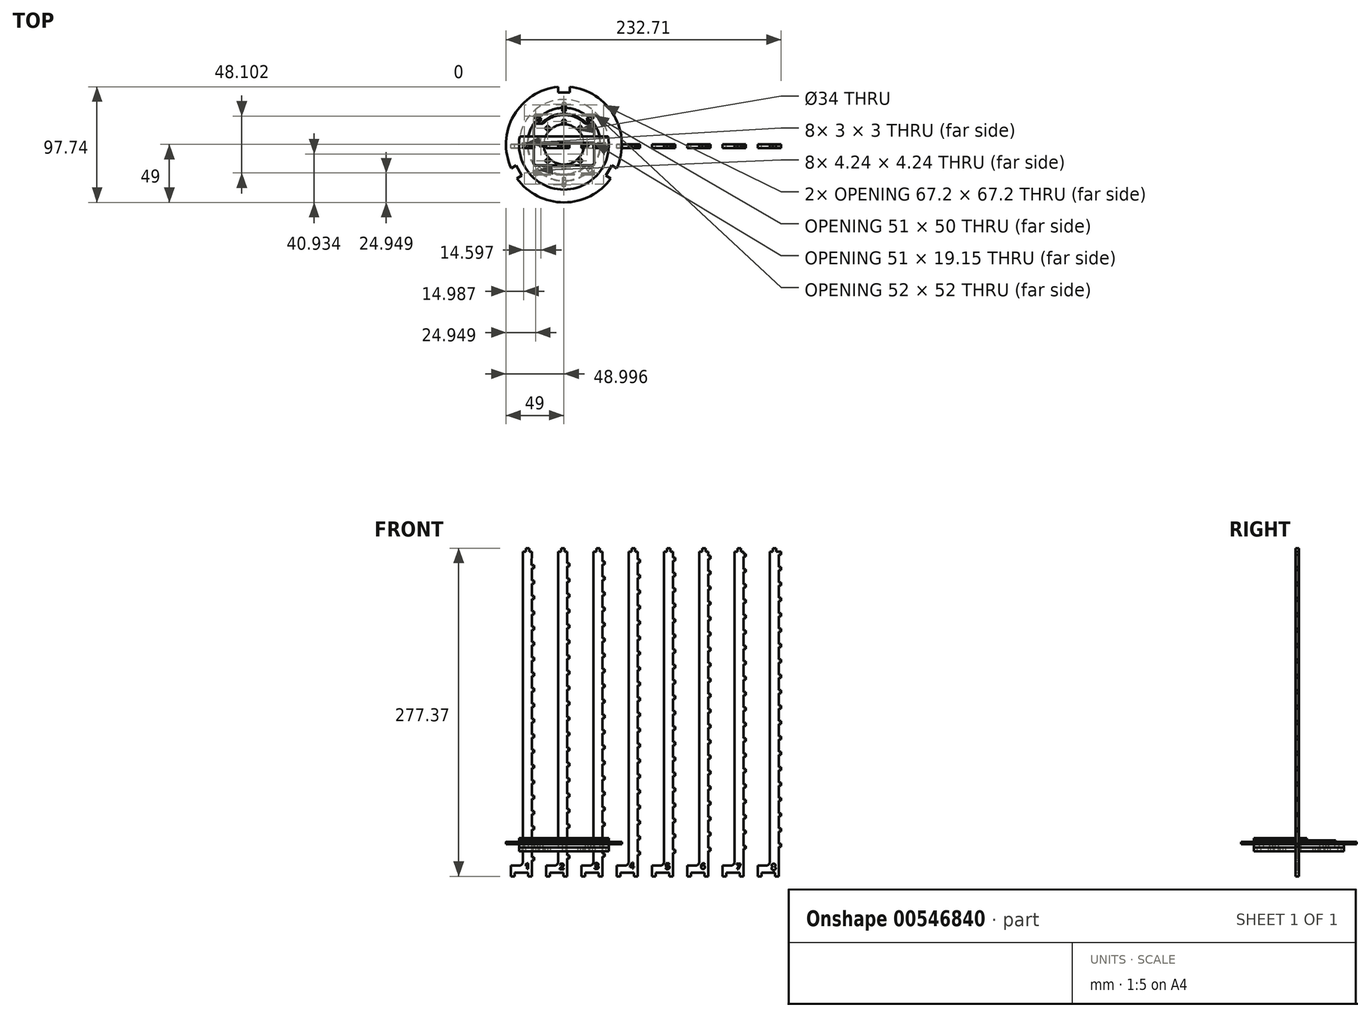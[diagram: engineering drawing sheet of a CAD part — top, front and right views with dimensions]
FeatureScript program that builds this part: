
annotation { "Feature Type Name" : "Feature", "Feature Type Description" : "" }
export const myFeature = defineFeature(function(context is Context, id is Id, definition is map)
    precondition{}
    {
        {
            assignVariable(context, id + "F0", {"name" : "thickness", "anyValue" : 3});
        }
        {
            var Q0;
            Q0=qCreatedBy(makeId("Front.planeOp"),FACE);
            var sketch = newSketch(context, id + "F1", { "sketchPlane" : qUnion([Q0])});
            skLineSegment(sketch, "E0", {"start": v(-27.17, -7.73) * mm, "end": v(-25.17, -7.73) * mm});
            skLineSegment(sketch, "E1", {"start": v(-25.17, -7.73) * mm, "end": v(-25.17, -5.23) * mm});
            skLineSegment(sketch, "E2", {"start": v(-25.17, -5.23) * mm, "end": v(-27.17, -5.23) * mm});
            skLineSegment(sketch, "E3.1.0.1", {"start": v(2.67, -6.1) * mm, "end": v(4.67, -6.1) * mm});
            skLineSegment(sketch, "E3.1.0.2", {"start": v(4.67, -6.1) * mm, "end": v(4.67, -3.6) * mm});
            skLineSegment(sketch, "E3.1.0.3", {"start": v(4.67, -3.6) * mm, "end": v(2.67, -3.6) * mm});
            skLineSegment(sketch, "E3.2.0.1", {"start": v(32.51, -4.48) * mm, "end": v(34.51, -4.48) * mm});
            skLineSegment(sketch, "E3.2.0.2", {"start": v(34.51, -4.48) * mm, "end": v(34.51, -1.98) * mm});
            skLineSegment(sketch, "E3.2.0.3", {"start": v(34.51, -1.98) * mm, "end": v(32.51, -1.98) * mm});
            skLineSegment(sketch, "E3.3.0.1", {"start": v(62.35, -2.86) * mm, "end": v(64.35, -2.86) * mm});
            skLineSegment(sketch, "E3.3.0.2", {"start": v(64.35, -2.86) * mm, "end": v(64.35, -0.36) * mm});
            skLineSegment(sketch, "E3.3.0.3", {"start": v(64.35, -0.36) * mm, "end": v(62.35, -0.36) * mm});
            skLineSegment(sketch, "E3.4.0.1", {"start": v(92.2, -1.23) * mm, "end": v(94.2, -1.23) * mm});
            skLineSegment(sketch, "E3.4.0.2", {"start": v(94.2, -1.23) * mm, "end": v(94.2, 1.27) * mm});
            skLineSegment(sketch, "E3.4.0.3", {"start": v(94.2, 1.27) * mm, "end": v(92.2, 1.27) * mm});
            skLineSegment(sketch, "E3.5.0.1", {"start": v(122.03, 0.4) * mm, "end": v(124.03, 0.4) * mm});
            skLineSegment(sketch, "E3.5.0.2", {"start": v(124.03, 0.4) * mm, "end": v(124.03, 2.9) * mm});
            skLineSegment(sketch, "E3.5.0.3", {"start": v(124.03, 2.9) * mm, "end": v(122.03, 2.9) * mm});
            skLineSegment(sketch, "E3.6.0.1", {"start": v(151.87, 2.02) * mm, "end": v(153.87, 2.02) * mm});
            skLineSegment(sketch, "E3.6.0.2", {"start": v(153.87, 2.02) * mm, "end": v(153.87, 4.52) * mm});
            skLineSegment(sketch, "E3.6.0.3", {"start": v(153.87, 4.52) * mm, "end": v(151.87, 4.52) * mm});
            skLineSegment(sketch, "E3.7.0.0", {"start": v(181.71, -18.23) * mm, "end": v(181.71, 3.64) * mm});
            skLineSegment(sketch, "E3.7.0.1", {"start": v(181.71, 3.64) * mm, "end": v(183.71, 3.64) * mm});
            skLineSegment(sketch, "E3.7.0.2", {"start": v(183.71, 3.64) * mm, "end": v(183.71, 6.14) * mm});
            skLineSegment(sketch, "E3.7.0.3", {"start": v(183.71, 6.14) * mm, "end": v(181.71, 6.14) * mm});
            skLineSegment(sketch, "E4.0.1.0", {"start": v(181.71, 6.14) * mm, "end": v(181.71, 16.64) * mm});
            skLineSegment(sketch, "E4.0.1.1", {"start": v(151.87, 4.52) * mm, "end": v(151.87, 15.02) * mm});
            skLineSegment(sketch, "E4.0.1.2", {"start": v(122.03, 2.9) * mm, "end": v(122.03, 13.4) * mm});
            skLineSegment(sketch, "E4.0.1.3", {"start": v(92.2, 1.27) * mm, "end": v(92.2, 11.77) * mm});
            skLineSegment(sketch, "E4.0.1.4", {"start": v(62.35, -0.36) * mm, "end": v(62.35, 10.14) * mm});
            skLineSegment(sketch, "E4.0.1.5", {"start": v(32.51, -1.98) * mm, "end": v(32.51, 8.52) * mm});
            skLineSegment(sketch, "E4.0.1.6", {"start": v(2.67, -3.6) * mm, "end": v(2.67, 6.9) * mm});
            skLineSegment(sketch, "E4.0.1.7", {"start": v(-27.17, -5.23) * mm, "end": v(-27.17, 5.27) * mm});
            skLineSegment(sketch, "E4.0.1.8", {"start": v(153.87, 17.52) * mm, "end": v(151.87, 17.52) * mm});
            skLineSegment(sketch, "E4.0.1.9", {"start": v(153.87, 15.02) * mm, "end": v(153.87, 17.52) * mm});
            skLineSegment(sketch, "E4.0.1.10", {"start": v(151.87, 15.02) * mm, "end": v(153.87, 15.02) * mm});
            skLineSegment(sketch, "E4.0.1.11", {"start": v(124.03, 15.9) * mm, "end": v(122.03, 15.9) * mm});
            skLineSegment(sketch, "E4.0.1.12", {"start": v(124.03, 13.4) * mm, "end": v(124.03, 15.9) * mm});
            skLineSegment(sketch, "E4.0.1.13", {"start": v(122.03, 13.4) * mm, "end": v(124.03, 13.4) * mm});
            skLineSegment(sketch, "E4.0.1.14", {"start": v(94.2, 14.27) * mm, "end": v(92.2, 14.27) * mm});
            skLineSegment(sketch, "E4.0.1.15", {"start": v(94.2, 11.77) * mm, "end": v(94.2, 14.27) * mm});
            skLineSegment(sketch, "E4.0.1.16", {"start": v(92.2, 11.77) * mm, "end": v(94.2, 11.77) * mm});
            skLineSegment(sketch, "E4.0.1.17", {"start": v(183.71, 19.14) * mm, "end": v(181.71, 19.14) * mm});
            skLineSegment(sketch, "E4.0.1.18", {"start": v(183.71, 16.64) * mm, "end": v(183.71, 19.14) * mm});
            skLineSegment(sketch, "E4.0.1.19", {"start": v(181.71, 16.64) * mm, "end": v(183.71, 16.64) * mm});
            skLineSegment(sketch, "E4.0.1.20", {"start": v(34.51, 11.02) * mm, "end": v(32.51, 11.02) * mm});
            skLineSegment(sketch, "E4.0.1.21", {"start": v(34.51, 8.52) * mm, "end": v(34.51, 11.02) * mm});
            skLineSegment(sketch, "E4.0.1.22", {"start": v(32.51, 8.52) * mm, "end": v(34.51, 8.52) * mm});
            skLineSegment(sketch, "E4.0.1.23", {"start": v(4.67, 9.4) * mm, "end": v(2.67, 9.4) * mm});
            skLineSegment(sketch, "E4.0.1.24", {"start": v(4.67, 6.9) * mm, "end": v(4.67, 9.4) * mm});
            skLineSegment(sketch, "E4.0.1.25", {"start": v(2.67, 6.9) * mm, "end": v(4.67, 6.9) * mm});
            skLineSegment(sketch, "E4.0.1.26", {"start": v(64.35, 12.64) * mm, "end": v(62.35, 12.64) * mm});
            skLineSegment(sketch, "E4.0.1.27", {"start": v(64.35, 10.14) * mm, "end": v(64.35, 12.64) * mm});
            skLineSegment(sketch, "E4.0.1.28", {"start": v(62.35, 10.14) * mm, "end": v(64.35, 10.14) * mm});
            skLineSegment(sketch, "E4.0.1.29", {"start": v(-25.17, 7.77) * mm, "end": v(-27.17, 7.77) * mm});
            skLineSegment(sketch, "E4.0.1.30", {"start": v(-25.17, 5.27) * mm, "end": v(-25.17, 7.77) * mm});
            skLineSegment(sketch, "E4.0.1.31", {"start": v(-27.17, 5.27) * mm, "end": v(-25.17, 5.27) * mm});
            skLineSegment(sketch, "E4.0.2.0", {"start": v(181.71, 19.14) * mm, "end": v(181.71, 29.64) * mm});
            skLineSegment(sketch, "E4.0.2.1", {"start": v(151.87, 17.52) * mm, "end": v(151.87, 28.02) * mm});
            skLineSegment(sketch, "E4.0.2.2", {"start": v(122.03, 15.9) * mm, "end": v(122.03, 26.4) * mm});
            skLineSegment(sketch, "E4.0.2.3", {"start": v(92.2, 14.27) * mm, "end": v(92.2, 24.77) * mm});
            skLineSegment(sketch, "E4.0.2.4", {"start": v(62.35, 12.64) * mm, "end": v(62.35, 23.14) * mm});
            skLineSegment(sketch, "E4.0.2.5", {"start": v(32.51, 11.02) * mm, "end": v(32.51, 21.52) * mm});
            skLineSegment(sketch, "E4.0.2.6", {"start": v(2.67, 9.4) * mm, "end": v(2.67, 19.9) * mm});
            skLineSegment(sketch, "E4.0.2.7", {"start": v(-27.17, 7.77) * mm, "end": v(-27.17, 18.27) * mm});
            skLineSegment(sketch, "E4.0.2.8", {"start": v(153.87, 30.52) * mm, "end": v(151.87, 30.52) * mm});
            skLineSegment(sketch, "E4.0.2.9", {"start": v(153.87, 28.02) * mm, "end": v(153.87, 30.52) * mm});
            skLineSegment(sketch, "E4.0.2.10", {"start": v(151.87, 28.02) * mm, "end": v(153.87, 28.02) * mm});
            skLineSegment(sketch, "E4.0.2.11", {"start": v(124.03, 28.9) * mm, "end": v(122.03, 28.9) * mm});
            skLineSegment(sketch, "E4.0.2.12", {"start": v(124.03, 26.4) * mm, "end": v(124.03, 28.9) * mm});
            skLineSegment(sketch, "E4.0.2.13", {"start": v(122.03, 26.4) * mm, "end": v(124.03, 26.4) * mm});
            skLineSegment(sketch, "E4.0.2.14", {"start": v(94.2, 27.27) * mm, "end": v(92.2, 27.27) * mm});
            skLineSegment(sketch, "E4.0.2.15", {"start": v(94.2, 24.77) * mm, "end": v(94.2, 27.27) * mm});
            skLineSegment(sketch, "E4.0.2.16", {"start": v(92.2, 24.77) * mm, "end": v(94.2, 24.77) * mm});
            skLineSegment(sketch, "E4.0.2.17", {"start": v(183.71, 32.14) * mm, "end": v(181.71, 32.14) * mm});
            skLineSegment(sketch, "E4.0.2.18", {"start": v(183.71, 29.64) * mm, "end": v(183.71, 32.14) * mm});
            skLineSegment(sketch, "E4.0.2.19", {"start": v(181.71, 29.64) * mm, "end": v(183.71, 29.64) * mm});
            skLineSegment(sketch, "E4.0.2.20", {"start": v(34.51, 24.02) * mm, "end": v(32.51, 24.02) * mm});
            skLineSegment(sketch, "E4.0.2.21", {"start": v(34.51, 21.52) * mm, "end": v(34.51, 24.02) * mm});
            skLineSegment(sketch, "E4.0.2.22", {"start": v(32.51, 21.52) * mm, "end": v(34.51, 21.52) * mm});
            skLineSegment(sketch, "E4.0.2.23", {"start": v(4.67, 22.4) * mm, "end": v(2.67, 22.4) * mm});
            skLineSegment(sketch, "E4.0.2.24", {"start": v(4.67, 19.9) * mm, "end": v(4.67, 22.4) * mm});
            skLineSegment(sketch, "E4.0.2.25", {"start": v(2.67, 19.9) * mm, "end": v(4.67, 19.9) * mm});
            skLineSegment(sketch, "E4.0.2.26", {"start": v(64.35, 25.64) * mm, "end": v(62.35, 25.64) * mm});
            skLineSegment(sketch, "E4.0.2.27", {"start": v(64.35, 23.14) * mm, "end": v(64.35, 25.64) * mm});
            skLineSegment(sketch, "E4.0.2.28", {"start": v(62.35, 23.14) * mm, "end": v(64.35, 23.14) * mm});
            skLineSegment(sketch, "E4.0.2.29", {"start": v(-25.17, 20.77) * mm, "end": v(-27.17, 20.77) * mm});
            skLineSegment(sketch, "E4.0.2.30", {"start": v(-25.17, 18.27) * mm, "end": v(-25.17, 20.77) * mm});
            skLineSegment(sketch, "E4.0.2.31", {"start": v(-27.17, 18.27) * mm, "end": v(-25.17, 18.27) * mm});
            skLineSegment(sketch, "E4.0.3.0", {"start": v(181.71, 32.14) * mm, "end": v(181.71, 42.64) * mm});
            skLineSegment(sketch, "E4.0.3.1", {"start": v(151.87, 30.52) * mm, "end": v(151.87, 41.02) * mm});
            skLineSegment(sketch, "E4.0.3.2", {"start": v(122.03, 28.9) * mm, "end": v(122.03, 39.4) * mm});
            skLineSegment(sketch, "E4.0.3.3", {"start": v(92.2, 27.27) * mm, "end": v(92.2, 37.77) * mm});
            skLineSegment(sketch, "E4.0.3.4", {"start": v(62.35, 25.64) * mm, "end": v(62.35, 36.14) * mm});
            skLineSegment(sketch, "E4.0.3.5", {"start": v(32.51, 24.02) * mm, "end": v(32.51, 34.52) * mm});
            skLineSegment(sketch, "E4.0.3.6", {"start": v(2.67, 22.4) * mm, "end": v(2.67, 32.9) * mm});
            skLineSegment(sketch, "E4.0.3.7", {"start": v(-27.17, 20.77) * mm, "end": v(-27.17, 31.27) * mm});
            skLineSegment(sketch, "E4.0.3.8", {"start": v(153.87, 43.52) * mm, "end": v(151.87, 43.52) * mm});
            skLineSegment(sketch, "E4.0.3.9", {"start": v(153.87, 41.02) * mm, "end": v(153.87, 43.52) * mm});
            skLineSegment(sketch, "E4.0.3.10", {"start": v(151.87, 41.02) * mm, "end": v(153.87, 41.02) * mm});
            skLineSegment(sketch, "E4.0.3.11", {"start": v(124.03, 41.9) * mm, "end": v(122.03, 41.9) * mm});
            skLineSegment(sketch, "E4.0.3.12", {"start": v(124.03, 39.4) * mm, "end": v(124.03, 41.9) * mm});
            skLineSegment(sketch, "E4.0.3.13", {"start": v(122.03, 39.4) * mm, "end": v(124.03, 39.4) * mm});
            skLineSegment(sketch, "E4.0.3.14", {"start": v(94.2, 40.27) * mm, "end": v(92.2, 40.27) * mm});
            skLineSegment(sketch, "E4.0.3.15", {"start": v(94.2, 37.77) * mm, "end": v(94.2, 40.27) * mm});
            skLineSegment(sketch, "E4.0.3.16", {"start": v(92.2, 37.77) * mm, "end": v(94.2, 37.77) * mm});
            skLineSegment(sketch, "E4.0.3.17", {"start": v(183.71, 45.14) * mm, "end": v(181.71, 45.14) * mm});
            skLineSegment(sketch, "E4.0.3.18", {"start": v(183.71, 42.64) * mm, "end": v(183.71, 45.14) * mm});
            skLineSegment(sketch, "E4.0.3.19", {"start": v(181.71, 42.64) * mm, "end": v(183.71, 42.64) * mm});
            skLineSegment(sketch, "E4.0.3.20", {"start": v(34.51, 37.02) * mm, "end": v(32.51, 37.02) * mm});
            skLineSegment(sketch, "E4.0.3.21", {"start": v(34.51, 34.52) * mm, "end": v(34.51, 37.02) * mm});
            skLineSegment(sketch, "E4.0.3.22", {"start": v(32.51, 34.52) * mm, "end": v(34.51, 34.52) * mm});
            skLineSegment(sketch, "E4.0.3.23", {"start": v(4.67, 35.4) * mm, "end": v(2.67, 35.4) * mm});
            skLineSegment(sketch, "E4.0.3.24", {"start": v(4.67, 32.9) * mm, "end": v(4.67, 35.4) * mm});
            skLineSegment(sketch, "E4.0.3.25", {"start": v(2.67, 32.9) * mm, "end": v(4.67, 32.9) * mm});
            skLineSegment(sketch, "E4.0.3.26", {"start": v(64.35, 38.64) * mm, "end": v(62.35, 38.64) * mm});
            skLineSegment(sketch, "E4.0.3.27", {"start": v(64.35, 36.14) * mm, "end": v(64.35, 38.64) * mm});
            skLineSegment(sketch, "E4.0.3.28", {"start": v(62.35, 36.14) * mm, "end": v(64.35, 36.14) * mm});
            skLineSegment(sketch, "E4.0.3.29", {"start": v(-25.17, 33.77) * mm, "end": v(-27.17, 33.77) * mm});
            skLineSegment(sketch, "E4.0.3.30", {"start": v(-25.17, 31.27) * mm, "end": v(-25.17, 33.77) * mm});
            skLineSegment(sketch, "E4.0.3.31", {"start": v(-27.17, 31.27) * mm, "end": v(-25.17, 31.27) * mm});
            skLineSegment(sketch, "E4.0.4.0", {"start": v(181.71, 45.14) * mm, "end": v(181.71, 55.64) * mm});
            skLineSegment(sketch, "E4.0.4.1", {"start": v(151.87, 43.52) * mm, "end": v(151.87, 54.02) * mm});
            skLineSegment(sketch, "E4.0.4.2", {"start": v(122.03, 41.9) * mm, "end": v(122.03, 52.4) * mm});
            skLineSegment(sketch, "E4.0.4.3", {"start": v(92.2, 40.27) * mm, "end": v(92.2, 50.77) * mm});
            skLineSegment(sketch, "E4.0.4.4", {"start": v(62.35, 38.64) * mm, "end": v(62.35, 49.14) * mm});
            skLineSegment(sketch, "E4.0.4.5", {"start": v(32.51, 37.02) * mm, "end": v(32.51, 47.52) * mm});
            skLineSegment(sketch, "E4.0.4.6", {"start": v(2.67, 35.4) * mm, "end": v(2.67, 45.9) * mm});
            skLineSegment(sketch, "E4.0.4.7", {"start": v(-27.17, 33.77) * mm, "end": v(-27.17, 44.27) * mm});
            skLineSegment(sketch, "E4.0.4.8", {"start": v(153.87, 56.52) * mm, "end": v(151.87, 56.52) * mm});
            skLineSegment(sketch, "E4.0.4.9", {"start": v(153.87, 54.02) * mm, "end": v(153.87, 56.52) * mm});
            skLineSegment(sketch, "E4.0.4.10", {"start": v(151.87, 54.02) * mm, "end": v(153.87, 54.02) * mm});
            skLineSegment(sketch, "E4.0.4.11", {"start": v(124.03, 54.9) * mm, "end": v(122.03, 54.9) * mm});
            skLineSegment(sketch, "E4.0.4.12", {"start": v(124.03, 52.4) * mm, "end": v(124.03, 54.9) * mm});
            skLineSegment(sketch, "E4.0.4.13", {"start": v(122.03, 52.4) * mm, "end": v(124.03, 52.4) * mm});
            skLineSegment(sketch, "E4.0.4.14", {"start": v(94.2, 53.27) * mm, "end": v(92.2, 53.27) * mm});
            skLineSegment(sketch, "E4.0.4.15", {"start": v(94.2, 50.77) * mm, "end": v(94.2, 53.27) * mm});
            skLineSegment(sketch, "E4.0.4.16", {"start": v(92.2, 50.77) * mm, "end": v(94.2, 50.77) * mm});
            skLineSegment(sketch, "E4.0.4.17", {"start": v(183.71, 58.14) * mm, "end": v(181.71, 58.14) * mm});
            skLineSegment(sketch, "E4.0.4.18", {"start": v(183.71, 55.64) * mm, "end": v(183.71, 58.14) * mm});
            skLineSegment(sketch, "E4.0.4.19", {"start": v(181.71, 55.64) * mm, "end": v(183.71, 55.64) * mm});
            skLineSegment(sketch, "E4.0.4.20", {"start": v(34.51, 50.02) * mm, "end": v(32.51, 50.02) * mm});
            skLineSegment(sketch, "E4.0.4.21", {"start": v(34.51, 47.52) * mm, "end": v(34.51, 50.02) * mm});
            skLineSegment(sketch, "E4.0.4.22", {"start": v(32.51, 47.52) * mm, "end": v(34.51, 47.52) * mm});
            skLineSegment(sketch, "E4.0.4.23", {"start": v(4.67, 48.4) * mm, "end": v(2.67, 48.4) * mm});
            skLineSegment(sketch, "E4.0.4.24", {"start": v(4.67, 45.9) * mm, "end": v(4.67, 48.4) * mm});
            skLineSegment(sketch, "E4.0.4.25", {"start": v(2.67, 45.9) * mm, "end": v(4.67, 45.9) * mm});
            skLineSegment(sketch, "E4.0.4.26", {"start": v(64.35, 51.64) * mm, "end": v(62.35, 51.64) * mm});
            skLineSegment(sketch, "E4.0.4.27", {"start": v(64.35, 49.14) * mm, "end": v(64.35, 51.64) * mm});
            skLineSegment(sketch, "E4.0.4.28", {"start": v(62.35, 49.14) * mm, "end": v(64.35, 49.14) * mm});
            skLineSegment(sketch, "E4.0.4.29", {"start": v(-25.17, 46.77) * mm, "end": v(-27.17, 46.77) * mm});
            skLineSegment(sketch, "E4.0.4.30", {"start": v(-25.17, 44.27) * mm, "end": v(-25.17, 46.77) * mm});
            skLineSegment(sketch, "E4.0.4.31", {"start": v(-27.17, 44.27) * mm, "end": v(-25.17, 44.27) * mm});
            skLineSegment(sketch, "E4.0.5.0", {"start": v(181.71, 58.14) * mm, "end": v(181.71, 68.64) * mm});
            skLineSegment(sketch, "E4.0.5.1", {"start": v(151.87, 56.52) * mm, "end": v(151.87, 67.02) * mm});
            skLineSegment(sketch, "E4.0.5.2", {"start": v(122.03, 54.9) * mm, "end": v(122.03, 65.4) * mm});
            skLineSegment(sketch, "E4.0.5.3", {"start": v(92.2, 53.27) * mm, "end": v(92.2, 63.77) * mm});
            skLineSegment(sketch, "E4.0.5.4", {"start": v(62.35, 51.64) * mm, "end": v(62.35, 62.14) * mm});
            skLineSegment(sketch, "E4.0.5.5", {"start": v(32.51, 50.02) * mm, "end": v(32.51, 60.52) * mm});
            skLineSegment(sketch, "E4.0.5.6", {"start": v(2.67, 48.4) * mm, "end": v(2.67, 58.9) * mm});
            skLineSegment(sketch, "E4.0.5.7", {"start": v(-27.17, 46.77) * mm, "end": v(-27.17, 57.27) * mm});
            skLineSegment(sketch, "E4.0.5.8", {"start": v(153.87, 69.52) * mm, "end": v(151.87, 69.52) * mm});
            skLineSegment(sketch, "E4.0.5.9", {"start": v(153.87, 67.02) * mm, "end": v(153.87, 69.52) * mm});
            skLineSegment(sketch, "E4.0.5.10", {"start": v(151.87, 67.02) * mm, "end": v(153.87, 67.02) * mm});
            skLineSegment(sketch, "E4.0.5.11", {"start": v(124.03, 67.9) * mm, "end": v(122.03, 67.9) * mm});
            skLineSegment(sketch, "E4.0.5.12", {"start": v(124.03, 65.4) * mm, "end": v(124.03, 67.9) * mm});
            skLineSegment(sketch, "E4.0.5.13", {"start": v(122.03, 65.4) * mm, "end": v(124.03, 65.4) * mm});
            skLineSegment(sketch, "E4.0.5.14", {"start": v(94.2, 66.27) * mm, "end": v(92.2, 66.27) * mm});
            skLineSegment(sketch, "E4.0.5.15", {"start": v(94.2, 63.77) * mm, "end": v(94.2, 66.27) * mm});
            skLineSegment(sketch, "E4.0.5.16", {"start": v(92.2, 63.77) * mm, "end": v(94.2, 63.77) * mm});
            skLineSegment(sketch, "E4.0.5.17", {"start": v(183.71, 71.14) * mm, "end": v(181.71, 71.14) * mm});
            skLineSegment(sketch, "E4.0.5.18", {"start": v(183.71, 68.64) * mm, "end": v(183.71, 71.14) * mm});
            skLineSegment(sketch, "E4.0.5.19", {"start": v(181.71, 68.64) * mm, "end": v(183.71, 68.64) * mm});
            skLineSegment(sketch, "E4.0.5.20", {"start": v(34.51, 63.02) * mm, "end": v(32.51, 63.02) * mm});
            skLineSegment(sketch, "E4.0.5.21", {"start": v(34.51, 60.52) * mm, "end": v(34.51, 63.02) * mm});
            skLineSegment(sketch, "E4.0.5.22", {"start": v(32.51, 60.52) * mm, "end": v(34.51, 60.52) * mm});
            skLineSegment(sketch, "E4.0.5.23", {"start": v(4.67, 61.4) * mm, "end": v(2.67, 61.4) * mm});
            skLineSegment(sketch, "E4.0.5.24", {"start": v(4.67, 58.9) * mm, "end": v(4.67, 61.4) * mm});
            skLineSegment(sketch, "E4.0.5.25", {"start": v(2.67, 58.9) * mm, "end": v(4.67, 58.9) * mm});
            skLineSegment(sketch, "E4.0.5.26", {"start": v(64.35, 64.64) * mm, "end": v(62.35, 64.64) * mm});
            skLineSegment(sketch, "E4.0.5.27", {"start": v(64.35, 62.14) * mm, "end": v(64.35, 64.64) * mm});
            skLineSegment(sketch, "E4.0.5.28", {"start": v(62.35, 62.14) * mm, "end": v(64.35, 62.14) * mm});
            skLineSegment(sketch, "E4.0.5.29", {"start": v(-25.17, 59.77) * mm, "end": v(-27.17, 59.77) * mm});
            skLineSegment(sketch, "E4.0.5.30", {"start": v(-25.17, 57.27) * mm, "end": v(-25.17, 59.77) * mm});
            skLineSegment(sketch, "E4.0.5.31", {"start": v(-27.17, 57.27) * mm, "end": v(-25.17, 57.27) * mm});
            skLineSegment(sketch, "E4.0.6.0", {"start": v(181.71, 71.14) * mm, "end": v(181.71, 81.64) * mm});
            skLineSegment(sketch, "E4.0.6.1", {"start": v(151.87, 69.52) * mm, "end": v(151.87, 80.02) * mm});
            skLineSegment(sketch, "E4.0.6.2", {"start": v(122.03, 67.9) * mm, "end": v(122.03, 78.4) * mm});
            skLineSegment(sketch, "E4.0.6.3", {"start": v(92.2, 66.27) * mm, "end": v(92.2, 76.77) * mm});
            skLineSegment(sketch, "E4.0.6.4", {"start": v(62.35, 64.64) * mm, "end": v(62.35, 75.14) * mm});
            skLineSegment(sketch, "E4.0.6.5", {"start": v(32.51, 63.02) * mm, "end": v(32.51, 73.52) * mm});
            skLineSegment(sketch, "E4.0.6.6", {"start": v(2.67, 61.4) * mm, "end": v(2.67, 71.9) * mm});
            skLineSegment(sketch, "E4.0.6.7", {"start": v(-27.17, 59.77) * mm, "end": v(-27.17, 70.27) * mm});
            skLineSegment(sketch, "E4.0.6.8", {"start": v(153.87, 82.52) * mm, "end": v(151.87, 82.52) * mm});
            skLineSegment(sketch, "E4.0.6.9", {"start": v(153.87, 80.02) * mm, "end": v(153.87, 82.52) * mm});
            skLineSegment(sketch, "E4.0.6.10", {"start": v(151.87, 80.02) * mm, "end": v(153.87, 80.02) * mm});
            skLineSegment(sketch, "E4.0.6.11", {"start": v(124.03, 80.9) * mm, "end": v(122.03, 80.9) * mm});
            skLineSegment(sketch, "E4.0.6.12", {"start": v(124.03, 78.4) * mm, "end": v(124.03, 80.9) * mm});
            skLineSegment(sketch, "E4.0.6.13", {"start": v(122.03, 78.4) * mm, "end": v(124.03, 78.4) * mm});
            skLineSegment(sketch, "E4.0.6.14", {"start": v(94.2, 79.27) * mm, "end": v(92.2, 79.27) * mm});
            skLineSegment(sketch, "E4.0.6.15", {"start": v(94.2, 76.77) * mm, "end": v(94.2, 79.27) * mm});
            skLineSegment(sketch, "E4.0.6.16", {"start": v(92.2, 76.77) * mm, "end": v(94.2, 76.77) * mm});
            skLineSegment(sketch, "E4.0.6.17", {"start": v(183.71, 84.14) * mm, "end": v(181.71, 84.14) * mm});
            skLineSegment(sketch, "E4.0.6.18", {"start": v(183.71, 81.64) * mm, "end": v(183.71, 84.14) * mm});
            skLineSegment(sketch, "E4.0.6.19", {"start": v(181.71, 81.64) * mm, "end": v(183.71, 81.64) * mm});
            skLineSegment(sketch, "E4.0.6.20", {"start": v(34.51, 76.02) * mm, "end": v(32.51, 76.02) * mm});
            skLineSegment(sketch, "E4.0.6.21", {"start": v(34.51, 73.52) * mm, "end": v(34.51, 76.02) * mm});
            skLineSegment(sketch, "E4.0.6.22", {"start": v(32.51, 73.52) * mm, "end": v(34.51, 73.52) * mm});
            skLineSegment(sketch, "E4.0.6.23", {"start": v(4.67, 74.4) * mm, "end": v(2.67, 74.4) * mm});
            skLineSegment(sketch, "E4.0.6.24", {"start": v(4.67, 71.9) * mm, "end": v(4.67, 74.4) * mm});
            skLineSegment(sketch, "E4.0.6.25", {"start": v(2.67, 71.9) * mm, "end": v(4.67, 71.9) * mm});
            skLineSegment(sketch, "E4.0.6.26", {"start": v(64.35, 77.64) * mm, "end": v(62.35, 77.64) * mm});
            skLineSegment(sketch, "E4.0.6.27", {"start": v(64.35, 75.14) * mm, "end": v(64.35, 77.64) * mm});
            skLineSegment(sketch, "E4.0.6.28", {"start": v(62.35, 75.14) * mm, "end": v(64.35, 75.14) * mm});
            skLineSegment(sketch, "E4.0.6.29", {"start": v(-25.17, 72.77) * mm, "end": v(-27.17, 72.77) * mm});
            skLineSegment(sketch, "E4.0.6.30", {"start": v(-25.17, 70.27) * mm, "end": v(-25.17, 72.77) * mm});
            skLineSegment(sketch, "E4.0.6.31", {"start": v(-27.17, 70.27) * mm, "end": v(-25.17, 70.27) * mm});
            skLineSegment(sketch, "E4.0.7.0", {"start": v(181.71, 84.14) * mm, "end": v(181.71, 94.64) * mm});
            skLineSegment(sketch, "E4.0.7.1", {"start": v(151.87, 82.52) * mm, "end": v(151.87, 93.02) * mm});
            skLineSegment(sketch, "E4.0.7.2", {"start": v(122.03, 80.9) * mm, "end": v(122.03, 91.4) * mm});
            skLineSegment(sketch, "E4.0.7.3", {"start": v(92.2, 79.27) * mm, "end": v(92.2, 89.77) * mm});
            skLineSegment(sketch, "E4.0.7.4", {"start": v(62.35, 77.64) * mm, "end": v(62.35, 88.14) * mm});
            skLineSegment(sketch, "E4.0.7.5", {"start": v(32.51, 76.02) * mm, "end": v(32.51, 86.52) * mm});
            skLineSegment(sketch, "E4.0.7.6", {"start": v(2.67, 74.4) * mm, "end": v(2.67, 84.9) * mm});
            skLineSegment(sketch, "E4.0.7.7", {"start": v(-27.17, 72.77) * mm, "end": v(-27.17, 83.27) * mm});
            skLineSegment(sketch, "E4.0.7.8", {"start": v(153.87, 95.52) * mm, "end": v(151.87, 95.52) * mm});
            skLineSegment(sketch, "E4.0.7.9", {"start": v(153.87, 93.02) * mm, "end": v(153.87, 95.52) * mm});
            skLineSegment(sketch, "E4.0.7.10", {"start": v(151.87, 93.02) * mm, "end": v(153.87, 93.02) * mm});
            skLineSegment(sketch, "E4.0.7.11", {"start": v(124.03, 93.9) * mm, "end": v(122.03, 93.9) * mm});
            skLineSegment(sketch, "E4.0.7.12", {"start": v(124.03, 91.4) * mm, "end": v(124.03, 93.9) * mm});
            skLineSegment(sketch, "E4.0.7.13", {"start": v(122.03, 91.4) * mm, "end": v(124.03, 91.4) * mm});
            skLineSegment(sketch, "E4.0.7.14", {"start": v(94.2, 92.27) * mm, "end": v(92.2, 92.27) * mm});
            skLineSegment(sketch, "E4.0.7.15", {"start": v(94.2, 89.77) * mm, "end": v(94.2, 92.27) * mm});
            skLineSegment(sketch, "E4.0.7.16", {"start": v(92.2, 89.77) * mm, "end": v(94.2, 89.77) * mm});
            skLineSegment(sketch, "E4.0.7.17", {"start": v(183.71, 97.14) * mm, "end": v(181.71, 97.14) * mm});
            skLineSegment(sketch, "E4.0.7.18", {"start": v(183.71, 94.64) * mm, "end": v(183.71, 97.14) * mm});
            skLineSegment(sketch, "E4.0.7.19", {"start": v(181.71, 94.64) * mm, "end": v(183.71, 94.64) * mm});
            skLineSegment(sketch, "E4.0.7.20", {"start": v(34.51, 89.02) * mm, "end": v(32.51, 89.02) * mm});
            skLineSegment(sketch, "E4.0.7.21", {"start": v(34.51, 86.52) * mm, "end": v(34.51, 89.02) * mm});
            skLineSegment(sketch, "E4.0.7.22", {"start": v(32.51, 86.52) * mm, "end": v(34.51, 86.52) * mm});
            skLineSegment(sketch, "E4.0.7.23", {"start": v(4.67, 87.4) * mm, "end": v(2.67, 87.4) * mm});
            skLineSegment(sketch, "E4.0.7.24", {"start": v(4.67, 84.9) * mm, "end": v(4.67, 87.4) * mm});
            skLineSegment(sketch, "E4.0.7.25", {"start": v(2.67, 84.9) * mm, "end": v(4.67, 84.9) * mm});
            skLineSegment(sketch, "E4.0.7.26", {"start": v(64.35, 90.64) * mm, "end": v(62.35, 90.64) * mm});
            skLineSegment(sketch, "E4.0.7.27", {"start": v(64.35, 88.14) * mm, "end": v(64.35, 90.64) * mm});
            skLineSegment(sketch, "E4.0.7.28", {"start": v(62.35, 88.14) * mm, "end": v(64.35, 88.14) * mm});
            skLineSegment(sketch, "E4.0.7.29", {"start": v(-25.17, 85.77) * mm, "end": v(-27.17, 85.77) * mm});
            skLineSegment(sketch, "E4.0.7.30", {"start": v(-25.17, 83.27) * mm, "end": v(-25.17, 85.77) * mm});
            skLineSegment(sketch, "E4.0.7.31", {"start": v(-27.17, 83.27) * mm, "end": v(-25.17, 83.27) * mm});
            skLineSegment(sketch, "E4.0.8.0", {"start": v(181.71, 97.14) * mm, "end": v(181.71, 107.64) * mm});
            skLineSegment(sketch, "E4.0.8.1", {"start": v(151.87, 95.52) * mm, "end": v(151.87, 106.02) * mm});
            skLineSegment(sketch, "E4.0.8.2", {"start": v(122.03, 93.9) * mm, "end": v(122.03, 104.4) * mm});
            skLineSegment(sketch, "E4.0.8.3", {"start": v(92.2, 92.27) * mm, "end": v(92.2, 102.77) * mm});
            skLineSegment(sketch, "E4.0.8.4", {"start": v(62.35, 90.64) * mm, "end": v(62.35, 101.14) * mm});
            skLineSegment(sketch, "E4.0.8.5", {"start": v(32.51, 89.02) * mm, "end": v(32.51, 99.52) * mm});
            skLineSegment(sketch, "E4.0.8.6", {"start": v(2.67, 87.4) * mm, "end": v(2.67, 97.9) * mm});
            skLineSegment(sketch, "E4.0.8.7", {"start": v(-27.17, 85.77) * mm, "end": v(-27.17, 96.27) * mm});
            skLineSegment(sketch, "E4.0.8.8", {"start": v(153.87, 108.52) * mm, "end": v(151.87, 108.52) * mm});
            skLineSegment(sketch, "E4.0.8.9", {"start": v(153.87, 106.02) * mm, "end": v(153.87, 108.52) * mm});
            skLineSegment(sketch, "E4.0.8.10", {"start": v(151.87, 106.02) * mm, "end": v(153.87, 106.02) * mm});
            skLineSegment(sketch, "E4.0.8.11", {"start": v(124.03, 106.9) * mm, "end": v(122.03, 106.9) * mm});
            skLineSegment(sketch, "E4.0.8.12", {"start": v(124.03, 104.4) * mm, "end": v(124.03, 106.9) * mm});
            skLineSegment(sketch, "E4.0.8.13", {"start": v(122.03, 104.4) * mm, "end": v(124.03, 104.4) * mm});
            skLineSegment(sketch, "E4.0.8.14", {"start": v(94.2, 105.27) * mm, "end": v(92.2, 105.27) * mm});
            skLineSegment(sketch, "E4.0.8.15", {"start": v(94.2, 102.77) * mm, "end": v(94.2, 105.27) * mm});
            skLineSegment(sketch, "E4.0.8.16", {"start": v(92.2, 102.77) * mm, "end": v(94.2, 102.77) * mm});
            skLineSegment(sketch, "E4.0.8.17", {"start": v(183.71, 110.14) * mm, "end": v(181.71, 110.14) * mm});
            skLineSegment(sketch, "E4.0.8.18", {"start": v(183.71, 107.64) * mm, "end": v(183.71, 110.14) * mm});
            skLineSegment(sketch, "E4.0.8.19", {"start": v(181.71, 107.64) * mm, "end": v(183.71, 107.64) * mm});
            skLineSegment(sketch, "E4.0.8.20", {"start": v(34.51, 102.02) * mm, "end": v(32.51, 102.02) * mm});
            skLineSegment(sketch, "E4.0.8.21", {"start": v(34.51, 99.52) * mm, "end": v(34.51, 102.02) * mm});
            skLineSegment(sketch, "E4.0.8.22", {"start": v(32.51, 99.52) * mm, "end": v(34.51, 99.52) * mm});
            skLineSegment(sketch, "E4.0.8.23", {"start": v(4.67, 100.4) * mm, "end": v(2.67, 100.4) * mm});
            skLineSegment(sketch, "E4.0.8.24", {"start": v(4.67, 97.9) * mm, "end": v(4.67, 100.4) * mm});
            skLineSegment(sketch, "E4.0.8.25", {"start": v(2.67, 97.9) * mm, "end": v(4.67, 97.9) * mm});
            skLineSegment(sketch, "E4.0.8.26", {"start": v(64.35, 103.64) * mm, "end": v(62.35, 103.64) * mm});
            skLineSegment(sketch, "E4.0.8.27", {"start": v(64.35, 101.14) * mm, "end": v(64.35, 103.64) * mm});
            skLineSegment(sketch, "E4.0.8.28", {"start": v(62.35, 101.14) * mm, "end": v(64.35, 101.14) * mm});
            skLineSegment(sketch, "E4.0.8.29", {"start": v(-25.17, 98.77) * mm, "end": v(-27.17, 98.77) * mm});
            skLineSegment(sketch, "E4.0.8.30", {"start": v(-25.17, 96.27) * mm, "end": v(-25.17, 98.77) * mm});
            skLineSegment(sketch, "E4.0.8.31", {"start": v(-27.17, 96.27) * mm, "end": v(-25.17, 96.27) * mm});
            skLineSegment(sketch, "E4.0.9.0", {"start": v(181.71, 110.14) * mm, "end": v(181.71, 120.64) * mm});
            skLineSegment(sketch, "E4.0.9.1", {"start": v(151.87, 108.52) * mm, "end": v(151.87, 119.02) * mm});
            skLineSegment(sketch, "E4.0.9.2", {"start": v(122.03, 106.9) * mm, "end": v(122.03, 117.4) * mm});
            skLineSegment(sketch, "E4.0.9.3", {"start": v(92.2, 105.27) * mm, "end": v(92.2, 115.77) * mm});
            skLineSegment(sketch, "E4.0.9.4", {"start": v(62.35, 103.64) * mm, "end": v(62.35, 114.14) * mm});
            skLineSegment(sketch, "E4.0.9.5", {"start": v(32.51, 102.02) * mm, "end": v(32.51, 112.52) * mm});
            skLineSegment(sketch, "E4.0.9.6", {"start": v(2.67, 100.4) * mm, "end": v(2.67, 110.9) * mm});
            skLineSegment(sketch, "E4.0.9.7", {"start": v(-27.17, 98.77) * mm, "end": v(-27.17, 109.27) * mm});
            skLineSegment(sketch, "E4.0.9.8", {"start": v(153.87, 121.52) * mm, "end": v(151.87, 121.52) * mm});
            skLineSegment(sketch, "E4.0.9.9", {"start": v(153.87, 119.02) * mm, "end": v(153.87, 121.52) * mm});
            skLineSegment(sketch, "E4.0.9.10", {"start": v(151.87, 119.02) * mm, "end": v(153.87, 119.02) * mm});
            skLineSegment(sketch, "E4.0.9.11", {"start": v(124.03, 119.9) * mm, "end": v(122.03, 119.9) * mm});
            skLineSegment(sketch, "E4.0.9.12", {"start": v(124.03, 117.4) * mm, "end": v(124.03, 119.9) * mm});
            skLineSegment(sketch, "E4.0.9.13", {"start": v(122.03, 117.4) * mm, "end": v(124.03, 117.4) * mm});
            skLineSegment(sketch, "E4.0.9.14", {"start": v(94.2, 118.27) * mm, "end": v(92.2, 118.27) * mm});
            skLineSegment(sketch, "E4.0.9.15", {"start": v(94.2, 115.77) * mm, "end": v(94.2, 118.27) * mm});
            skLineSegment(sketch, "E4.0.9.16", {"start": v(92.2, 115.77) * mm, "end": v(94.2, 115.77) * mm});
            skLineSegment(sketch, "E4.0.9.17", {"start": v(183.71, 123.14) * mm, "end": v(181.71, 123.14) * mm});
            skLineSegment(sketch, "E4.0.9.18", {"start": v(183.71, 120.64) * mm, "end": v(183.71, 123.14) * mm});
            skLineSegment(sketch, "E4.0.9.19", {"start": v(181.71, 120.64) * mm, "end": v(183.71, 120.64) * mm});
            skLineSegment(sketch, "E4.0.9.20", {"start": v(34.51, 115.02) * mm, "end": v(32.51, 115.02) * mm});
            skLineSegment(sketch, "E4.0.9.21", {"start": v(34.51, 112.52) * mm, "end": v(34.51, 115.02) * mm});
            skLineSegment(sketch, "E4.0.9.22", {"start": v(32.51, 112.52) * mm, "end": v(34.51, 112.52) * mm});
            skLineSegment(sketch, "E4.0.9.23", {"start": v(4.67, 113.4) * mm, "end": v(2.67, 113.4) * mm});
            skLineSegment(sketch, "E4.0.9.24", {"start": v(4.67, 110.9) * mm, "end": v(4.67, 113.4) * mm});
            skLineSegment(sketch, "E4.0.9.25", {"start": v(2.67, 110.9) * mm, "end": v(4.67, 110.9) * mm});
            skLineSegment(sketch, "E4.0.9.26", {"start": v(64.35, 116.64) * mm, "end": v(62.35, 116.64) * mm});
            skLineSegment(sketch, "E4.0.9.27", {"start": v(64.35, 114.14) * mm, "end": v(64.35, 116.64) * mm});
            skLineSegment(sketch, "E4.0.9.28", {"start": v(62.35, 114.14) * mm, "end": v(64.35, 114.14) * mm});
            skLineSegment(sketch, "E4.0.9.29", {"start": v(-25.17, 111.77) * mm, "end": v(-27.17, 111.77) * mm});
            skLineSegment(sketch, "E4.0.9.30", {"start": v(-25.17, 109.27) * mm, "end": v(-25.17, 111.77) * mm});
            skLineSegment(sketch, "E4.0.9.31", {"start": v(-27.17, 109.27) * mm, "end": v(-25.17, 109.27) * mm});
            skLineSegment(sketch, "E4.0.10.0", {"start": v(181.71, 123.14) * mm, "end": v(181.71, 133.64) * mm});
            skLineSegment(sketch, "E4.0.10.1", {"start": v(151.87, 121.52) * mm, "end": v(151.87, 132.02) * mm});
            skLineSegment(sketch, "E4.0.10.2", {"start": v(122.03, 119.9) * mm, "end": v(122.03, 130.4) * mm});
            skLineSegment(sketch, "E4.0.10.3", {"start": v(92.2, 118.27) * mm, "end": v(92.2, 128.77) * mm});
            skLineSegment(sketch, "E4.0.10.4", {"start": v(62.35, 116.64) * mm, "end": v(62.35, 127.14) * mm});
            skLineSegment(sketch, "E4.0.10.5", {"start": v(32.51, 115.02) * mm, "end": v(32.51, 125.52) * mm});
            skLineSegment(sketch, "E4.0.10.6", {"start": v(2.67, 113.4) * mm, "end": v(2.67, 123.9) * mm});
            skLineSegment(sketch, "E4.0.10.7", {"start": v(-27.17, 111.77) * mm, "end": v(-27.17, 122.27) * mm});
            skLineSegment(sketch, "E4.0.10.8", {"start": v(153.87, 134.52) * mm, "end": v(151.87, 134.52) * mm});
            skLineSegment(sketch, "E4.0.10.9", {"start": v(153.87, 132.02) * mm, "end": v(153.87, 134.52) * mm});
            skLineSegment(sketch, "E4.0.10.10", {"start": v(151.87, 132.02) * mm, "end": v(153.87, 132.02) * mm});
            skLineSegment(sketch, "E4.0.10.11", {"start": v(124.03, 132.9) * mm, "end": v(122.03, 132.9) * mm});
            skLineSegment(sketch, "E4.0.10.12", {"start": v(124.03, 130.4) * mm, "end": v(124.03, 132.9) * mm});
            skLineSegment(sketch, "E4.0.10.13", {"start": v(122.03, 130.4) * mm, "end": v(124.03, 130.4) * mm});
            skLineSegment(sketch, "E4.0.10.14", {"start": v(94.2, 131.27) * mm, "end": v(92.2, 131.27) * mm});
            skLineSegment(sketch, "E4.0.10.15", {"start": v(94.2, 128.77) * mm, "end": v(94.2, 131.27) * mm});
            skLineSegment(sketch, "E4.0.10.16", {"start": v(92.2, 128.77) * mm, "end": v(94.2, 128.77) * mm});
            skLineSegment(sketch, "E4.0.10.17", {"start": v(183.71, 136.14) * mm, "end": v(181.71, 136.14) * mm});
            skLineSegment(sketch, "E4.0.10.18", {"start": v(183.71, 133.64) * mm, "end": v(183.71, 136.14) * mm});
            skLineSegment(sketch, "E4.0.10.19", {"start": v(181.71, 133.64) * mm, "end": v(183.71, 133.64) * mm});
            skLineSegment(sketch, "E4.0.10.20", {"start": v(34.51, 128.02) * mm, "end": v(32.51, 128.02) * mm});
            skLineSegment(sketch, "E4.0.10.21", {"start": v(34.51, 125.52) * mm, "end": v(34.51, 128.02) * mm});
            skLineSegment(sketch, "E4.0.10.22", {"start": v(32.51, 125.52) * mm, "end": v(34.51, 125.52) * mm});
            skLineSegment(sketch, "E4.0.10.23", {"start": v(4.67, 126.4) * mm, "end": v(2.67, 126.4) * mm});
            skLineSegment(sketch, "E4.0.10.24", {"start": v(4.67, 123.9) * mm, "end": v(4.67, 126.4) * mm});
            skLineSegment(sketch, "E4.0.10.25", {"start": v(2.67, 123.9) * mm, "end": v(4.67, 123.9) * mm});
            skLineSegment(sketch, "E4.0.10.26", {"start": v(64.35, 129.64) * mm, "end": v(62.35, 129.64) * mm});
            skLineSegment(sketch, "E4.0.10.27", {"start": v(64.35, 127.14) * mm, "end": v(64.35, 129.64) * mm});
            skLineSegment(sketch, "E4.0.10.28", {"start": v(62.35, 127.14) * mm, "end": v(64.35, 127.14) * mm});
            skLineSegment(sketch, "E4.0.10.29", {"start": v(-25.17, 124.77) * mm, "end": v(-27.17, 124.77) * mm});
            skLineSegment(sketch, "E4.0.10.30", {"start": v(-25.17, 122.27) * mm, "end": v(-25.17, 124.77) * mm});
            skLineSegment(sketch, "E4.0.10.31", {"start": v(-27.17, 122.27) * mm, "end": v(-25.17, 122.27) * mm});
            skLineSegment(sketch, "E4.0.11.0", {"start": v(181.71, 136.14) * mm, "end": v(181.71, 146.64) * mm});
            skLineSegment(sketch, "E4.0.11.1", {"start": v(151.87, 134.52) * mm, "end": v(151.87, 145.02) * mm});
            skLineSegment(sketch, "E4.0.11.2", {"start": v(122.03, 132.9) * mm, "end": v(122.03, 143.4) * mm});
            skLineSegment(sketch, "E4.0.11.3", {"start": v(92.2, 131.27) * mm, "end": v(92.2, 141.77) * mm});
            skLineSegment(sketch, "E4.0.11.4", {"start": v(62.35, 129.64) * mm, "end": v(62.35, 140.14) * mm});
            skLineSegment(sketch, "E4.0.11.5", {"start": v(32.51, 128.02) * mm, "end": v(32.51, 138.52) * mm});
            skLineSegment(sketch, "E4.0.11.6", {"start": v(2.67, 126.4) * mm, "end": v(2.67, 136.9) * mm});
            skLineSegment(sketch, "E4.0.11.7", {"start": v(-27.17, 124.77) * mm, "end": v(-27.17, 135.27) * mm});
            skLineSegment(sketch, "E4.0.11.8", {"start": v(153.87, 147.52) * mm, "end": v(151.87, 147.52) * mm});
            skLineSegment(sketch, "E4.0.11.9", {"start": v(153.87, 145.02) * mm, "end": v(153.87, 147.52) * mm});
            skLineSegment(sketch, "E4.0.11.10", {"start": v(151.87, 145.02) * mm, "end": v(153.87, 145.02) * mm});
            skLineSegment(sketch, "E4.0.11.11", {"start": v(124.03, 145.9) * mm, "end": v(122.03, 145.9) * mm});
            skLineSegment(sketch, "E4.0.11.12", {"start": v(124.03, 143.4) * mm, "end": v(124.03, 145.9) * mm});
            skLineSegment(sketch, "E4.0.11.13", {"start": v(122.03, 143.4) * mm, "end": v(124.03, 143.4) * mm});
            skLineSegment(sketch, "E4.0.11.14", {"start": v(94.2, 144.27) * mm, "end": v(92.2, 144.27) * mm});
            skLineSegment(sketch, "E4.0.11.15", {"start": v(94.2, 141.77) * mm, "end": v(94.2, 144.27) * mm});
            skLineSegment(sketch, "E4.0.11.16", {"start": v(92.2, 141.77) * mm, "end": v(94.2, 141.77) * mm});
            skLineSegment(sketch, "E4.0.11.17", {"start": v(183.71, 149.14) * mm, "end": v(181.71, 149.14) * mm});
            skLineSegment(sketch, "E4.0.11.18", {"start": v(183.71, 146.64) * mm, "end": v(183.71, 149.14) * mm});
            skLineSegment(sketch, "E4.0.11.19", {"start": v(181.71, 146.64) * mm, "end": v(183.71, 146.64) * mm});
            skLineSegment(sketch, "E4.0.11.20", {"start": v(34.51, 141.02) * mm, "end": v(32.51, 141.02) * mm});
            skLineSegment(sketch, "E4.0.11.21", {"start": v(34.51, 138.52) * mm, "end": v(34.51, 141.02) * mm});
            skLineSegment(sketch, "E4.0.11.22", {"start": v(32.51, 138.52) * mm, "end": v(34.51, 138.52) * mm});
            skLineSegment(sketch, "E4.0.11.23", {"start": v(4.67, 139.4) * mm, "end": v(2.67, 139.4) * mm});
            skLineSegment(sketch, "E4.0.11.24", {"start": v(4.67, 136.9) * mm, "end": v(4.67, 139.4) * mm});
            skLineSegment(sketch, "E4.0.11.25", {"start": v(2.67, 136.9) * mm, "end": v(4.67, 136.9) * mm});
            skLineSegment(sketch, "E4.0.11.26", {"start": v(64.35, 142.64) * mm, "end": v(62.35, 142.64) * mm});
            skLineSegment(sketch, "E4.0.11.27", {"start": v(64.35, 140.14) * mm, "end": v(64.35, 142.64) * mm});
            skLineSegment(sketch, "E4.0.11.28", {"start": v(62.35, 140.14) * mm, "end": v(64.35, 140.14) * mm});
            skLineSegment(sketch, "E4.0.11.29", {"start": v(-25.17, 137.77) * mm, "end": v(-27.17, 137.77) * mm});
            skLineSegment(sketch, "E4.0.11.30", {"start": v(-25.17, 135.27) * mm, "end": v(-25.17, 137.77) * mm});
            skLineSegment(sketch, "E4.0.11.31", {"start": v(-27.17, 135.27) * mm, "end": v(-25.17, 135.27) * mm});
            skLineSegment(sketch, "E4.0.12.0", {"start": v(181.71, 149.14) * mm, "end": v(181.71, 159.64) * mm});
            skLineSegment(sketch, "E4.0.12.1", {"start": v(151.87, 147.52) * mm, "end": v(151.87, 158.02) * mm});
            skLineSegment(sketch, "E4.0.12.2", {"start": v(122.03, 145.9) * mm, "end": v(122.03, 156.4) * mm});
            skLineSegment(sketch, "E4.0.12.3", {"start": v(92.2, 144.27) * mm, "end": v(92.2, 154.77) * mm});
            skLineSegment(sketch, "E4.0.12.4", {"start": v(62.35, 142.64) * mm, "end": v(62.35, 153.14) * mm});
            skLineSegment(sketch, "E4.0.12.5", {"start": v(32.51, 141.02) * mm, "end": v(32.51, 151.52) * mm});
            skLineSegment(sketch, "E4.0.12.6", {"start": v(2.67, 139.4) * mm, "end": v(2.67, 149.9) * mm});
            skLineSegment(sketch, "E4.0.12.7", {"start": v(-27.17, 137.77) * mm, "end": v(-27.17, 148.27) * mm});
            skLineSegment(sketch, "E4.0.12.8", {"start": v(153.87, 160.52) * mm, "end": v(151.87, 160.52) * mm});
            skLineSegment(sketch, "E4.0.12.9", {"start": v(153.87, 158.02) * mm, "end": v(153.87, 160.52) * mm});
            skLineSegment(sketch, "E4.0.12.10", {"start": v(151.87, 158.02) * mm, "end": v(153.87, 158.02) * mm});
            skLineSegment(sketch, "E4.0.12.11", {"start": v(124.03, 158.9) * mm, "end": v(122.03, 158.9) * mm});
            skLineSegment(sketch, "E4.0.12.12", {"start": v(124.03, 156.4) * mm, "end": v(124.03, 158.9) * mm});
            skLineSegment(sketch, "E4.0.12.13", {"start": v(122.03, 156.4) * mm, "end": v(124.03, 156.4) * mm});
            skLineSegment(sketch, "E4.0.12.14", {"start": v(94.2, 157.27) * mm, "end": v(92.2, 157.27) * mm});
            skLineSegment(sketch, "E4.0.12.15", {"start": v(94.2, 154.77) * mm, "end": v(94.2, 157.27) * mm});
            skLineSegment(sketch, "E4.0.12.16", {"start": v(92.2, 154.77) * mm, "end": v(94.2, 154.77) * mm});
            skLineSegment(sketch, "E4.0.12.17", {"start": v(183.71, 162.14) * mm, "end": v(181.71, 162.14) * mm});
            skLineSegment(sketch, "E4.0.12.18", {"start": v(183.71, 159.64) * mm, "end": v(183.71, 162.14) * mm});
            skLineSegment(sketch, "E4.0.12.19", {"start": v(181.71, 159.64) * mm, "end": v(183.71, 159.64) * mm});
            skLineSegment(sketch, "E4.0.12.20", {"start": v(34.51, 154.02) * mm, "end": v(32.51, 154.02) * mm});
            skLineSegment(sketch, "E4.0.12.21", {"start": v(34.51, 151.52) * mm, "end": v(34.51, 154.02) * mm});
            skLineSegment(sketch, "E4.0.12.22", {"start": v(32.51, 151.52) * mm, "end": v(34.51, 151.52) * mm});
            skLineSegment(sketch, "E4.0.12.23", {"start": v(4.67, 152.4) * mm, "end": v(2.67, 152.4) * mm});
            skLineSegment(sketch, "E4.0.12.24", {"start": v(4.67, 149.9) * mm, "end": v(4.67, 152.4) * mm});
            skLineSegment(sketch, "E4.0.12.25", {"start": v(2.67, 149.9) * mm, "end": v(4.67, 149.9) * mm});
            skLineSegment(sketch, "E4.0.12.26", {"start": v(64.35, 155.64) * mm, "end": v(62.35, 155.64) * mm});
            skLineSegment(sketch, "E4.0.12.27", {"start": v(64.35, 153.14) * mm, "end": v(64.35, 155.64) * mm});
            skLineSegment(sketch, "E4.0.12.28", {"start": v(62.35, 153.14) * mm, "end": v(64.35, 153.14) * mm});
            skLineSegment(sketch, "E4.0.12.29", {"start": v(-25.17, 150.77) * mm, "end": v(-27.17, 150.77) * mm});
            skLineSegment(sketch, "E4.0.12.30", {"start": v(-25.17, 148.27) * mm, "end": v(-25.17, 150.77) * mm});
            skLineSegment(sketch, "E4.0.12.31", {"start": v(-27.17, 148.27) * mm, "end": v(-25.17, 148.27) * mm});
            skLineSegment(sketch, "E4.0.13.0", {"start": v(181.71, 162.14) * mm, "end": v(181.71, 172.64) * mm});
            skLineSegment(sketch, "E4.0.13.1", {"start": v(151.87, 160.52) * mm, "end": v(151.87, 171.02) * mm});
            skLineSegment(sketch, "E4.0.13.2", {"start": v(122.03, 158.9) * mm, "end": v(122.03, 169.4) * mm});
            skLineSegment(sketch, "E4.0.13.3", {"start": v(92.2, 157.27) * mm, "end": v(92.2, 167.77) * mm});
            skLineSegment(sketch, "E4.0.13.4", {"start": v(62.35, 155.64) * mm, "end": v(62.35, 166.14) * mm});
            skLineSegment(sketch, "E4.0.13.5", {"start": v(32.51, 154.02) * mm, "end": v(32.51, 164.52) * mm});
            skLineSegment(sketch, "E4.0.13.6", {"start": v(2.67, 152.4) * mm, "end": v(2.67, 162.9) * mm});
            skLineSegment(sketch, "E4.0.13.7", {"start": v(-27.17, 150.77) * mm, "end": v(-27.17, 161.27) * mm});
            skLineSegment(sketch, "E4.0.13.8", {"start": v(153.87, 173.52) * mm, "end": v(151.87, 173.52) * mm});
            skLineSegment(sketch, "E4.0.13.9", {"start": v(153.87, 171.02) * mm, "end": v(153.87, 173.52) * mm});
            skLineSegment(sketch, "E4.0.13.10", {"start": v(151.87, 171.02) * mm, "end": v(153.87, 171.02) * mm});
            skLineSegment(sketch, "E4.0.13.11", {"start": v(124.03, 171.9) * mm, "end": v(122.03, 171.9) * mm});
            skLineSegment(sketch, "E4.0.13.12", {"start": v(124.03, 169.4) * mm, "end": v(124.03, 171.9) * mm});
            skLineSegment(sketch, "E4.0.13.13", {"start": v(122.03, 169.4) * mm, "end": v(124.03, 169.4) * mm});
            skLineSegment(sketch, "E4.0.13.14", {"start": v(94.2, 170.27) * mm, "end": v(92.2, 170.27) * mm});
            skLineSegment(sketch, "E4.0.13.15", {"start": v(94.2, 167.77) * mm, "end": v(94.2, 170.27) * mm});
            skLineSegment(sketch, "E4.0.13.16", {"start": v(92.2, 167.77) * mm, "end": v(94.2, 167.77) * mm});
            skLineSegment(sketch, "E4.0.13.17", {"start": v(183.71, 175.14) * mm, "end": v(181.71, 175.14) * mm});
            skLineSegment(sketch, "E4.0.13.18", {"start": v(183.71, 172.64) * mm, "end": v(183.71, 175.14) * mm});
            skLineSegment(sketch, "E4.0.13.19", {"start": v(181.71, 172.64) * mm, "end": v(183.71, 172.64) * mm});
            skLineSegment(sketch, "E4.0.13.20", {"start": v(34.51, 167.02) * mm, "end": v(32.51, 167.02) * mm});
            skLineSegment(sketch, "E4.0.13.21", {"start": v(34.51, 164.52) * mm, "end": v(34.51, 167.02) * mm});
            skLineSegment(sketch, "E4.0.13.22", {"start": v(32.51, 164.52) * mm, "end": v(34.51, 164.52) * mm});
            skLineSegment(sketch, "E4.0.13.23", {"start": v(4.67, 165.4) * mm, "end": v(2.67, 165.4) * mm});
            skLineSegment(sketch, "E4.0.13.24", {"start": v(4.67, 162.9) * mm, "end": v(4.67, 165.4) * mm});
            skLineSegment(sketch, "E4.0.13.25", {"start": v(2.67, 162.9) * mm, "end": v(4.67, 162.9) * mm});
            skLineSegment(sketch, "E4.0.13.26", {"start": v(64.35, 168.64) * mm, "end": v(62.35, 168.64) * mm});
            skLineSegment(sketch, "E4.0.13.27", {"start": v(64.35, 166.14) * mm, "end": v(64.35, 168.64) * mm});
            skLineSegment(sketch, "E4.0.13.28", {"start": v(62.35, 166.14) * mm, "end": v(64.35, 166.14) * mm});
            skLineSegment(sketch, "E4.0.13.29", {"start": v(-25.17, 163.77) * mm, "end": v(-27.17, 163.77) * mm});
            skLineSegment(sketch, "E4.0.13.30", {"start": v(-25.17, 161.27) * mm, "end": v(-25.17, 163.77) * mm});
            skLineSegment(sketch, "E4.0.13.31", {"start": v(-27.17, 161.27) * mm, "end": v(-25.17, 161.27) * mm});
            skLineSegment(sketch, "E4.0.14.0", {"start": v(181.71, 175.14) * mm, "end": v(181.71, 185.64) * mm});
            skLineSegment(sketch, "E4.0.14.1", {"start": v(151.87, 173.52) * mm, "end": v(151.87, 184.02) * mm});
            skLineSegment(sketch, "E4.0.14.2", {"start": v(122.03, 171.9) * mm, "end": v(122.03, 182.4) * mm});
            skLineSegment(sketch, "E4.0.14.3", {"start": v(92.2, 170.27) * mm, "end": v(92.2, 180.77) * mm});
            skLineSegment(sketch, "E4.0.14.4", {"start": v(62.35, 168.64) * mm, "end": v(62.35, 179.14) * mm});
            skLineSegment(sketch, "E4.0.14.5", {"start": v(32.51, 167.02) * mm, "end": v(32.51, 177.52) * mm});
            skLineSegment(sketch, "E4.0.14.6", {"start": v(2.67, 165.4) * mm, "end": v(2.67, 175.9) * mm});
            skLineSegment(sketch, "E4.0.14.7", {"start": v(-27.17, 163.77) * mm, "end": v(-27.17, 174.27) * mm});
            skLineSegment(sketch, "E4.0.14.8", {"start": v(153.87, 186.52) * mm, "end": v(151.87, 186.52) * mm});
            skLineSegment(sketch, "E4.0.14.9", {"start": v(153.87, 184.02) * mm, "end": v(153.87, 186.52) * mm});
            skLineSegment(sketch, "E4.0.14.10", {"start": v(151.87, 184.02) * mm, "end": v(153.87, 184.02) * mm});
            skLineSegment(sketch, "E4.0.14.11", {"start": v(124.03, 184.9) * mm, "end": v(122.03, 184.9) * mm});
            skLineSegment(sketch, "E4.0.14.12", {"start": v(124.03, 182.4) * mm, "end": v(124.03, 184.9) * mm});
            skLineSegment(sketch, "E4.0.14.13", {"start": v(122.03, 182.4) * mm, "end": v(124.03, 182.4) * mm});
            skLineSegment(sketch, "E4.0.14.14", {"start": v(94.2, 183.27) * mm, "end": v(92.2, 183.27) * mm});
            skLineSegment(sketch, "E4.0.14.15", {"start": v(94.2, 180.77) * mm, "end": v(94.2, 183.27) * mm});
            skLineSegment(sketch, "E4.0.14.16", {"start": v(92.2, 180.77) * mm, "end": v(94.2, 180.77) * mm});
            skLineSegment(sketch, "E4.0.14.17", {"start": v(183.71, 188.14) * mm, "end": v(181.71, 188.14) * mm});
            skLineSegment(sketch, "E4.0.14.18", {"start": v(183.71, 185.64) * mm, "end": v(183.71, 188.14) * mm});
            skLineSegment(sketch, "E4.0.14.19", {"start": v(181.71, 185.64) * mm, "end": v(183.71, 185.64) * mm});
            skLineSegment(sketch, "E4.0.14.20", {"start": v(34.51, 180.02) * mm, "end": v(32.51, 180.02) * mm});
            skLineSegment(sketch, "E4.0.14.21", {"start": v(34.51, 177.52) * mm, "end": v(34.51, 180.02) * mm});
            skLineSegment(sketch, "E4.0.14.22", {"start": v(32.51, 177.52) * mm, "end": v(34.51, 177.52) * mm});
            skLineSegment(sketch, "E4.0.14.23", {"start": v(4.67, 178.4) * mm, "end": v(2.67, 178.4) * mm});
            skLineSegment(sketch, "E4.0.14.24", {"start": v(4.67, 175.9) * mm, "end": v(4.67, 178.4) * mm});
            skLineSegment(sketch, "E4.0.14.25", {"start": v(2.67, 175.9) * mm, "end": v(4.67, 175.9) * mm});
            skLineSegment(sketch, "E4.0.14.26", {"start": v(64.35, 181.64) * mm, "end": v(62.35, 181.64) * mm});
            skLineSegment(sketch, "E4.0.14.27", {"start": v(64.35, 179.14) * mm, "end": v(64.35, 181.64) * mm});
            skLineSegment(sketch, "E4.0.14.28", {"start": v(62.35, 179.14) * mm, "end": v(64.35, 179.14) * mm});
            skLineSegment(sketch, "E4.0.14.29", {"start": v(-25.17, 176.77) * mm, "end": v(-27.17, 176.77) * mm});
            skLineSegment(sketch, "E4.0.14.30", {"start": v(-25.17, 174.27) * mm, "end": v(-25.17, 176.77) * mm});
            skLineSegment(sketch, "E4.0.14.31", {"start": v(-27.17, 174.27) * mm, "end": v(-25.17, 174.27) * mm});
            skLineSegment(sketch, "E4.0.15.0", {"start": v(181.71, 188.14) * mm, "end": v(181.71, 198.64) * mm});
            skLineSegment(sketch, "E4.0.15.1", {"start": v(151.87, 186.52) * mm, "end": v(151.87, 197.02) * mm});
            skLineSegment(sketch, "E4.0.15.2", {"start": v(122.03, 184.9) * mm, "end": v(122.03, 195.4) * mm});
            skLineSegment(sketch, "E4.0.15.3", {"start": v(92.2, 183.27) * mm, "end": v(92.2, 193.77) * mm});
            skLineSegment(sketch, "E4.0.15.4", {"start": v(62.35, 181.64) * mm, "end": v(62.35, 192.14) * mm});
            skLineSegment(sketch, "E4.0.15.5", {"start": v(32.51, 180.02) * mm, "end": v(32.51, 190.52) * mm});
            skLineSegment(sketch, "E4.0.15.6", {"start": v(2.67, 178.4) * mm, "end": v(2.67, 188.9) * mm});
            skLineSegment(sketch, "E4.0.15.7", {"start": v(-27.17, 176.77) * mm, "end": v(-27.17, 187.27) * mm});
            skLineSegment(sketch, "E4.0.15.8", {"start": v(153.87, 199.52) * mm, "end": v(151.87, 199.52) * mm});
            skLineSegment(sketch, "E4.0.15.9", {"start": v(153.87, 197.02) * mm, "end": v(153.87, 199.52) * mm});
            skLineSegment(sketch, "E4.0.15.10", {"start": v(151.87, 197.02) * mm, "end": v(153.87, 197.02) * mm});
            skLineSegment(sketch, "E4.0.15.11", {"start": v(124.03, 197.9) * mm, "end": v(122.03, 197.9) * mm});
            skLineSegment(sketch, "E4.0.15.12", {"start": v(124.03, 195.4) * mm, "end": v(124.03, 197.9) * mm});
            skLineSegment(sketch, "E4.0.15.13", {"start": v(122.03, 195.4) * mm, "end": v(124.03, 195.4) * mm});
            skLineSegment(sketch, "E4.0.15.14", {"start": v(94.2, 196.27) * mm, "end": v(92.2, 196.27) * mm});
            skLineSegment(sketch, "E4.0.15.15", {"start": v(94.2, 193.77) * mm, "end": v(94.2, 196.27) * mm});
            skLineSegment(sketch, "E4.0.15.16", {"start": v(92.2, 193.77) * mm, "end": v(94.2, 193.77) * mm});
            skLineSegment(sketch, "E4.0.15.17", {"start": v(183.71, 201.14) * mm, "end": v(181.71, 201.14) * mm});
            skLineSegment(sketch, "E4.0.15.18", {"start": v(183.71, 198.64) * mm, "end": v(183.71, 201.14) * mm});
            skLineSegment(sketch, "E4.0.15.19", {"start": v(181.71, 198.64) * mm, "end": v(183.71, 198.64) * mm});
            skLineSegment(sketch, "E4.0.15.20", {"start": v(34.51, 193.02) * mm, "end": v(32.51, 193.02) * mm});
            skLineSegment(sketch, "E4.0.15.21", {"start": v(34.51, 190.52) * mm, "end": v(34.51, 193.02) * mm});
            skLineSegment(sketch, "E4.0.15.22", {"start": v(32.51, 190.52) * mm, "end": v(34.51, 190.52) * mm});
            skLineSegment(sketch, "E4.0.15.23", {"start": v(4.67, 191.4) * mm, "end": v(2.67, 191.4) * mm});
            skLineSegment(sketch, "E4.0.15.24", {"start": v(4.67, 188.9) * mm, "end": v(4.67, 191.4) * mm});
            skLineSegment(sketch, "E4.0.15.25", {"start": v(2.67, 188.9) * mm, "end": v(4.67, 188.9) * mm});
            skLineSegment(sketch, "E4.0.15.26", {"start": v(64.35, 194.64) * mm, "end": v(62.35, 194.64) * mm});
            skLineSegment(sketch, "E4.0.15.27", {"start": v(64.35, 192.14) * mm, "end": v(64.35, 194.64) * mm});
            skLineSegment(sketch, "E4.0.15.28", {"start": v(62.35, 192.14) * mm, "end": v(64.35, 192.14) * mm});
            skLineSegment(sketch, "E4.0.15.29", {"start": v(-25.17, 189.77) * mm, "end": v(-27.17, 189.77) * mm});
            skLineSegment(sketch, "E4.0.15.30", {"start": v(-25.17, 187.27) * mm, "end": v(-25.17, 189.77) * mm});
            skLineSegment(sketch, "E4.0.15.31", {"start": v(-27.17, 187.27) * mm, "end": v(-25.17, 187.27) * mm});
            skLineSegment(sketch, "E4.0.16.0", {"start": v(181.71, 201.14) * mm, "end": v(181.71, 211.64) * mm});
            skLineSegment(sketch, "E4.0.16.1", {"start": v(151.87, 199.52) * mm, "end": v(151.87, 210.02) * mm});
            skLineSegment(sketch, "E4.0.16.2", {"start": v(122.03, 197.9) * mm, "end": v(122.03, 208.4) * mm});
            skLineSegment(sketch, "E4.0.16.3", {"start": v(92.2, 196.27) * mm, "end": v(92.2, 206.77) * mm});
            skLineSegment(sketch, "E4.0.16.4", {"start": v(62.35, 194.64) * mm, "end": v(62.35, 205.14) * mm});
            skLineSegment(sketch, "E4.0.16.5", {"start": v(32.51, 193.02) * mm, "end": v(32.51, 203.52) * mm});
            skLineSegment(sketch, "E4.0.16.6", {"start": v(2.67, 191.4) * mm, "end": v(2.67, 201.9) * mm});
            skLineSegment(sketch, "E4.0.16.7", {"start": v(-27.17, 189.77) * mm, "end": v(-27.17, 200.27) * mm});
            skLineSegment(sketch, "E4.0.16.8", {"start": v(153.87, 212.52) * mm, "end": v(151.87, 212.52) * mm});
            skLineSegment(sketch, "E4.0.16.9", {"start": v(153.87, 210.02) * mm, "end": v(153.87, 212.52) * mm});
            skLineSegment(sketch, "E4.0.16.10", {"start": v(151.87, 210.02) * mm, "end": v(153.87, 210.02) * mm});
            skLineSegment(sketch, "E4.0.16.11", {"start": v(124.03, 210.9) * mm, "end": v(122.03, 210.9) * mm});
            skLineSegment(sketch, "E4.0.16.12", {"start": v(124.03, 208.4) * mm, "end": v(124.03, 210.9) * mm});
            skLineSegment(sketch, "E4.0.16.13", {"start": v(122.03, 208.4) * mm, "end": v(124.03, 208.4) * mm});
            skLineSegment(sketch, "E4.0.16.14", {"start": v(94.2, 209.27) * mm, "end": v(92.2, 209.27) * mm});
            skLineSegment(sketch, "E4.0.16.15", {"start": v(94.2, 206.77) * mm, "end": v(94.2, 209.27) * mm});
            skLineSegment(sketch, "E4.0.16.16", {"start": v(92.2, 206.77) * mm, "end": v(94.2, 206.77) * mm});
            skLineSegment(sketch, "E4.0.16.17", {"start": v(183.71, 214.14) * mm, "end": v(181.71, 214.14) * mm});
            skLineSegment(sketch, "E4.0.16.18", {"start": v(183.71, 211.64) * mm, "end": v(183.71, 214.14) * mm});
            skLineSegment(sketch, "E4.0.16.19", {"start": v(181.71, 211.64) * mm, "end": v(183.71, 211.64) * mm});
            skLineSegment(sketch, "E4.0.16.20", {"start": v(34.51, 206.02) * mm, "end": v(32.51, 206.02) * mm});
            skLineSegment(sketch, "E4.0.16.21", {"start": v(34.51, 203.52) * mm, "end": v(34.51, 206.02) * mm});
            skLineSegment(sketch, "E4.0.16.22", {"start": v(32.51, 203.52) * mm, "end": v(34.51, 203.52) * mm});
            skLineSegment(sketch, "E4.0.16.23", {"start": v(4.67, 204.4) * mm, "end": v(2.67, 204.4) * mm});
            skLineSegment(sketch, "E4.0.16.24", {"start": v(4.67, 201.9) * mm, "end": v(4.67, 204.4) * mm});
            skLineSegment(sketch, "E4.0.16.25", {"start": v(2.67, 201.9) * mm, "end": v(4.67, 201.9) * mm});
            skLineSegment(sketch, "E4.0.16.26", {"start": v(64.35, 207.64) * mm, "end": v(62.35, 207.64) * mm});
            skLineSegment(sketch, "E4.0.16.27", {"start": v(64.35, 205.14) * mm, "end": v(64.35, 207.64) * mm});
            skLineSegment(sketch, "E4.0.16.28", {"start": v(62.35, 205.14) * mm, "end": v(64.35, 205.14) * mm});
            skLineSegment(sketch, "E4.0.16.29", {"start": v(-25.17, 202.77) * mm, "end": v(-27.17, 202.77) * mm});
            skLineSegment(sketch, "E4.0.16.30", {"start": v(-25.17, 200.27) * mm, "end": v(-25.17, 202.77) * mm});
            skLineSegment(sketch, "E4.0.16.31", {"start": v(-27.17, 200.27) * mm, "end": v(-25.17, 200.27) * mm});
            skLineSegment(sketch, "E4.0.17.0", {"start": v(181.71, 214.14) * mm, "end": v(181.71, 224.64) * mm});
            skLineSegment(sketch, "E4.0.17.1", {"start": v(151.87, 212.52) * mm, "end": v(151.87, 223.02) * mm});
            skLineSegment(sketch, "E4.0.17.2", {"start": v(122.03, 210.9) * mm, "end": v(122.03, 221.4) * mm});
            skLineSegment(sketch, "E4.0.17.3", {"start": v(92.2, 209.27) * mm, "end": v(92.2, 219.77) * mm});
            skLineSegment(sketch, "E4.0.17.4", {"start": v(62.35, 207.64) * mm, "end": v(62.35, 218.14) * mm});
            skLineSegment(sketch, "E4.0.17.5", {"start": v(32.51, 206.02) * mm, "end": v(32.51, 216.52) * mm});
            skLineSegment(sketch, "E4.0.17.6", {"start": v(2.67, 204.4) * mm, "end": v(2.67, 214.9) * mm});
            skLineSegment(sketch, "E4.0.17.7", {"start": v(-27.17, 202.77) * mm, "end": v(-27.17, 213.27) * mm});
            skLineSegment(sketch, "E4.0.17.8", {"start": v(153.87, 225.52) * mm, "end": v(151.87, 225.52) * mm});
            skLineSegment(sketch, "E4.0.17.9", {"start": v(153.87, 223.02) * mm, "end": v(153.87, 225.52) * mm});
            skLineSegment(sketch, "E4.0.17.10", {"start": v(151.87, 223.02) * mm, "end": v(153.87, 223.02) * mm});
            skLineSegment(sketch, "E4.0.17.11", {"start": v(124.03, 223.9) * mm, "end": v(122.03, 223.9) * mm});
            skLineSegment(sketch, "E4.0.17.12", {"start": v(124.03, 221.4) * mm, "end": v(124.03, 223.9) * mm});
            skLineSegment(sketch, "E4.0.17.13", {"start": v(122.03, 221.4) * mm, "end": v(124.03, 221.4) * mm});
            skLineSegment(sketch, "E4.0.17.14", {"start": v(94.2, 222.27) * mm, "end": v(92.2, 222.27) * mm});
            skLineSegment(sketch, "E4.0.17.15", {"start": v(94.2, 219.77) * mm, "end": v(94.2, 222.27) * mm});
            skLineSegment(sketch, "E4.0.17.16", {"start": v(92.2, 219.77) * mm, "end": v(94.2, 219.77) * mm});
            skLineSegment(sketch, "E4.0.17.17", {"start": v(183.71, 227.14) * mm, "end": v(181.71, 227.14) * mm});
            skLineSegment(sketch, "E4.0.17.18", {"start": v(183.71, 224.64) * mm, "end": v(183.71, 227.14) * mm});
            skLineSegment(sketch, "E4.0.17.19", {"start": v(181.71, 224.64) * mm, "end": v(183.71, 224.64) * mm});
            skLineSegment(sketch, "E4.0.17.20", {"start": v(34.51, 219.02) * mm, "end": v(32.51, 219.02) * mm});
            skLineSegment(sketch, "E4.0.17.21", {"start": v(34.51, 216.52) * mm, "end": v(34.51, 219.02) * mm});
            skLineSegment(sketch, "E4.0.17.22", {"start": v(32.51, 216.52) * mm, "end": v(34.51, 216.52) * mm});
            skLineSegment(sketch, "E4.0.17.23", {"start": v(4.67, 217.4) * mm, "end": v(2.67, 217.4) * mm});
            skLineSegment(sketch, "E4.0.17.24", {"start": v(4.67, 214.9) * mm, "end": v(4.67, 217.4) * mm});
            skLineSegment(sketch, "E4.0.17.25", {"start": v(2.67, 214.9) * mm, "end": v(4.67, 214.9) * mm});
            skLineSegment(sketch, "E4.0.17.26", {"start": v(64.35, 220.64) * mm, "end": v(62.35, 220.64) * mm});
            skLineSegment(sketch, "E4.0.17.27", {"start": v(64.35, 218.14) * mm, "end": v(64.35, 220.64) * mm});
            skLineSegment(sketch, "E4.0.17.28", {"start": v(62.35, 218.14) * mm, "end": v(64.35, 218.14) * mm});
            skLineSegment(sketch, "E4.0.17.29", {"start": v(-25.17, 215.77) * mm, "end": v(-27.17, 215.77) * mm});
            skLineSegment(sketch, "E4.0.17.30", {"start": v(-25.17, 213.27) * mm, "end": v(-25.17, 215.77) * mm});
            skLineSegment(sketch, "E4.0.17.31", {"start": v(-27.17, 213.27) * mm, "end": v(-25.17, 213.27) * mm});
            skLineSegment(sketch, "E4.0.18.0", {"start": v(181.71, 227.14) * mm, "end": v(181.71, 237.64) * mm});
            skLineSegment(sketch, "E4.0.18.1", {"start": v(151.87, 225.52) * mm, "end": v(151.87, 236.02) * mm});
            skLineSegment(sketch, "E4.0.18.2", {"start": v(122.03, 223.9) * mm, "end": v(122.03, 234.4) * mm});
            skLineSegment(sketch, "E4.0.18.3", {"start": v(92.2, 222.27) * mm, "end": v(92.2, 232.77) * mm});
            skLineSegment(sketch, "E4.0.18.4", {"start": v(62.35, 220.64) * mm, "end": v(62.35, 231.14) * mm});
            skLineSegment(sketch, "E4.0.18.5", {"start": v(32.51, 219.02) * mm, "end": v(32.51, 229.52) * mm});
            skLineSegment(sketch, "E4.0.18.6", {"start": v(2.67, 217.4) * mm, "end": v(2.67, 227.9) * mm});
            skLineSegment(sketch, "E4.0.18.7", {"start": v(-27.17, 215.77) * mm, "end": v(-27.17, 226.27) * mm});
            skLineSegment(sketch, "E4.0.18.8", {"start": v(153.87, 238.52) * mm, "end": v(151.87, 238.52) * mm});
            skLineSegment(sketch, "E4.0.18.9", {"start": v(153.87, 236.02) * mm, "end": v(153.87, 238.52) * mm});
            skLineSegment(sketch, "E4.0.18.10", {"start": v(151.87, 236.02) * mm, "end": v(153.87, 236.02) * mm});
            skLineSegment(sketch, "E4.0.18.11", {"start": v(124.03, 236.9) * mm, "end": v(122.03, 236.9) * mm});
            skLineSegment(sketch, "E4.0.18.12", {"start": v(124.03, 234.4) * mm, "end": v(124.03, 236.9) * mm});
            skLineSegment(sketch, "E4.0.18.13", {"start": v(122.03, 234.4) * mm, "end": v(124.03, 234.4) * mm});
            skLineSegment(sketch, "E4.0.18.14", {"start": v(94.2, 235.27) * mm, "end": v(92.2, 235.27) * mm});
            skLineSegment(sketch, "E4.0.18.15", {"start": v(94.2, 232.77) * mm, "end": v(94.2, 235.27) * mm});
            skLineSegment(sketch, "E4.0.18.16", {"start": v(92.2, 232.77) * mm, "end": v(94.2, 232.77) * mm});
            skLineSegment(sketch, "E4.0.18.17", {"start": v(183.71, 240.14) * mm, "end": v(181.71, 240.14) * mm});
            skLineSegment(sketch, "E4.0.18.18", {"start": v(183.71, 237.64) * mm, "end": v(183.71, 240.14) * mm});
            skLineSegment(sketch, "E4.0.18.19", {"start": v(181.71, 237.64) * mm, "end": v(183.71, 237.64) * mm});
            skLineSegment(sketch, "E4.0.18.20", {"start": v(34.51, 232.02) * mm, "end": v(32.51, 232.02) * mm});
            skLineSegment(sketch, "E4.0.18.21", {"start": v(34.51, 229.52) * mm, "end": v(34.51, 232.02) * mm});
            skLineSegment(sketch, "E4.0.18.22", {"start": v(32.51, 229.52) * mm, "end": v(34.51, 229.52) * mm});
            skLineSegment(sketch, "E4.0.18.23", {"start": v(4.67, 230.4) * mm, "end": v(2.67, 230.4) * mm});
            skLineSegment(sketch, "E4.0.18.24", {"start": v(4.67, 227.9) * mm, "end": v(4.67, 230.4) * mm});
            skLineSegment(sketch, "E4.0.18.25", {"start": v(2.67, 227.9) * mm, "end": v(4.67, 227.9) * mm});
            skLineSegment(sketch, "E4.0.18.26", {"start": v(64.35, 233.64) * mm, "end": v(62.35, 233.64) * mm});
            skLineSegment(sketch, "E4.0.18.27", {"start": v(64.35, 231.14) * mm, "end": v(64.35, 233.64) * mm});
            skLineSegment(sketch, "E4.0.18.28", {"start": v(62.35, 231.14) * mm, "end": v(64.35, 231.14) * mm});
            skLineSegment(sketch, "E4.0.18.29", {"start": v(-25.17, 228.77) * mm, "end": v(-27.17, 228.77) * mm});
            skLineSegment(sketch, "E4.0.18.30", {"start": v(-25.17, 226.27) * mm, "end": v(-25.17, 228.77) * mm});
            skLineSegment(sketch, "E4.0.18.31", {"start": v(-27.17, 226.27) * mm, "end": v(-25.17, 226.27) * mm});
            skLineSegment(sketch, "E4.0.19.0", {"start": v(181.71, 240.14) * mm, "end": v(181.71, 250.64) * mm});
            skLineSegment(sketch, "E4.0.19.1", {"start": v(151.87, 238.52) * mm, "end": v(151.87, 249.02) * mm});
            skLineSegment(sketch, "E4.0.19.2", {"start": v(122.03, 236.9) * mm, "end": v(122.03, 247.4) * mm});
            skLineSegment(sketch, "E4.0.19.3", {"start": v(92.2, 235.27) * mm, "end": v(92.2, 245.77) * mm});
            skLineSegment(sketch, "E4.0.19.4", {"start": v(62.35, 233.64) * mm, "end": v(62.35, 244.14) * mm});
            skLineSegment(sketch, "E4.0.19.5", {"start": v(32.51, 232.02) * mm, "end": v(32.51, 242.52) * mm});
            skLineSegment(sketch, "E4.0.19.6", {"start": v(2.67, 230.4) * mm, "end": v(2.67, 240.9) * mm});
            skLineSegment(sketch, "E4.0.19.7", {"start": v(-27.17, 228.77) * mm, "end": v(-27.17, 239.27) * mm});
            skLineSegment(sketch, "E4.0.19.8", {"start": v(153.87, 251.52) * mm, "end": v(151.87, 251.52) * mm});
            skLineSegment(sketch, "E4.0.19.9", {"start": v(153.87, 249.02) * mm, "end": v(153.87, 251.52) * mm});
            skLineSegment(sketch, "E4.0.19.10", {"start": v(151.87, 249.02) * mm, "end": v(153.87, 249.02) * mm});
            skLineSegment(sketch, "E4.0.19.11", {"start": v(124.03, 249.9) * mm, "end": v(122.03, 249.9) * mm});
            skLineSegment(sketch, "E4.0.19.12", {"start": v(124.03, 247.4) * mm, "end": v(124.03, 249.9) * mm});
            skLineSegment(sketch, "E4.0.19.13", {"start": v(122.03, 247.4) * mm, "end": v(124.03, 247.4) * mm});
            skLineSegment(sketch, "E4.0.19.14", {"start": v(94.2, 248.27) * mm, "end": v(92.2, 248.27) * mm});
            skLineSegment(sketch, "E4.0.19.15", {"start": v(94.2, 245.77) * mm, "end": v(94.2, 248.27) * mm});
            skLineSegment(sketch, "E4.0.19.16", {"start": v(92.2, 245.77) * mm, "end": v(94.2, 245.77) * mm});
            skLineSegment(sketch, "E4.0.19.18", {"start": v(183.71, 250.64) * mm, "end": v(183.71, 253.14) * mm});
            skLineSegment(sketch, "E4.0.19.19", {"start": v(181.71, 250.64) * mm, "end": v(183.71, 250.64) * mm});
            skLineSegment(sketch, "E4.0.19.20", {"start": v(34.51, 245.02) * mm, "end": v(32.51, 245.02) * mm});
            skLineSegment(sketch, "E4.0.19.21", {"start": v(34.51, 242.52) * mm, "end": v(34.51, 245.02) * mm});
            skLineSegment(sketch, "E4.0.19.22", {"start": v(32.51, 242.52) * mm, "end": v(34.51, 242.52) * mm});
            skLineSegment(sketch, "E4.0.19.23", {"start": v(4.67, 243.4) * mm, "end": v(2.67, 243.4) * mm});
            skLineSegment(sketch, "E4.0.19.24", {"start": v(4.67, 240.9) * mm, "end": v(4.67, 243.4) * mm});
            skLineSegment(sketch, "E4.0.19.25", {"start": v(2.67, 240.9) * mm, "end": v(4.67, 240.9) * mm});
            skLineSegment(sketch, "E4.0.19.26", {"start": v(64.35, 246.64) * mm, "end": v(62.35, 246.64) * mm});
            skLineSegment(sketch, "E4.0.19.27", {"start": v(64.35, 244.14) * mm, "end": v(64.35, 246.64) * mm});
            skLineSegment(sketch, "E4.0.19.28", {"start": v(62.35, 244.14) * mm, "end": v(64.35, 244.14) * mm});
            skLineSegment(sketch, "E4.0.19.30", {"start": v(-25.17, 239.27) * mm, "end": v(-25.17, 241.77) * mm});
            skLineSegment(sketch, "E4.0.19.31", {"start": v(-27.17, 239.27) * mm, "end": v(-25.17, 239.27) * mm});
            skLineSegment(sketch, "E5", {"start": v(-27.17, 253.14) * mm, "end": v(-27.26, 241.77) * mm});
            skLineSegment(sketch, "E6", {"start": v(2.67, 243.4) * mm, "end": v(2.67, 253.14) * mm});
            skLineSegment(sketch, "E7", {"start": v(32.51, 245.02) * mm, "end": v(32.51, 253.14) * mm});
            skLineSegment(sketch, "E8", {"start": v(62.35, 246.64) * mm, "end": v(62.35, 253.14) * mm});
            skLineSegment(sketch, "E9", {"start": v(92.2, 248.27) * mm, "end": v(92.2, 253.14) * mm});
            skLineSegment(sketch, "E10", {"start": v(122.03, 249.9) * mm, "end": v(122.03, 253.14) * mm});
            skLineSegment(sketch, "E11", {"start": v(151.87, 251.52) * mm, "end": v(151.87, 253.14) * mm});
            skLineSegment(sketch, "E12", {"start": v(174.12, 253.14) * mm, "end": v(174.12, -9.16) * mm});
            skLineSegment(sketch, "E13", {"start": v(181.71, -18.23) * mm, "end": v(181.71, -6.86) * mm});
            skLineSegment(sketch, "E14", {"start": v(171.12, -12.16) * mm, "end": v(164.12, -12.16) * mm});
            skLineSegment(sketch, "E15", {"start": v(164.12, -12.16) * mm, "end": v(164.12, -18.23) * mm});
            skLineSegment(sketch, "E16", {"start": v(-27.17, -7.73) * mm, "end": v(-27.17, -5.23) * mm, "construction": true});
            skLineSegment(sketch, "E17.trimOffspring", {"start": v(167.12, -18.23) * mm, "end": v(178.71, -18.23) * mm});
            skPoint(sketch, "E18.visualSharp", {"position": v(174.12, -12.16) * mm});
            skArc(sketch, "E18.filletArc", {"start": v(171.12, -12.16) * mm, "mid": v(173.24, -11.28) * mm, "end": v(174.12, -9.16) * mm});
            skLineSegment(sketch, "E19", {"start": v(164.12, -18.23) * mm, "end": v(164.12, -21.23) * mm});
            skLineSegment(sketch, "E20", {"start": v(164.12, -21.23) * mm, "end": v(167.12, -21.23) * mm});
            skLineSegment(sketch, "E21", {"start": v(167.12, -21.23) * mm, "end": v(167.12, -18.23) * mm});
            skLineSegment(sketch, "E22", {"start": v(181.71, -18.23) * mm, "end": v(181.71, -21.23) * mm});
            skLineSegment(sketch, "E23", {"start": v(181.71, -21.23) * mm, "end": v(178.71, -21.23) * mm});
            skLineSegment(sketch, "E24", {"start": v(178.71, -21.23) * mm, "end": v(178.71, -18.23) * mm});
            skLineSegment(sketch, "E25", {"start": v(183.71, 253.14) * mm, "end": v(179.62, 253.14) * mm});
            skPoint(sketch, "E26.orphan", {"position": v(174.12, 251.14) * mm});
            skPoint(sketch, "E27.orphan", {"position": v(181.24, 6.14) * mm});
            skLineSegment(sketch, "E28.1.0.0", {"start": v(151.87, -21.23) * mm, "end": v(148.87, -21.23) * mm});
            skLineSegment(sketch, "E28.1.0.2", {"start": v(148.87, -21.23) * mm, "end": v(148.87, -18.23) * mm});
            skLineSegment(sketch, "E28.1.0.3", {"start": v(137.28, -18.23) * mm, "end": v(148.87, -18.23) * mm});
            skLineSegment(sketch, "E28.1.0.4", {"start": v(137.28, -21.23) * mm, "end": v(137.28, -18.23) * mm});
            skLineSegment(sketch, "E28.1.0.5", {"start": v(134.28, -21.23) * mm, "end": v(137.28, -21.23) * mm});
            skLineSegment(sketch, "E28.1.0.6", {"start": v(134.28, -18.23) * mm, "end": v(134.28, -21.23) * mm});
            skLineSegment(sketch, "E28.1.0.7", {"start": v(134.28, -12.16) * mm, "end": v(134.28, -18.23) * mm});
            skLineSegment(sketch, "E28.1.0.8", {"start": v(141.28, -12.16) * mm, "end": v(134.28, -12.16) * mm});
            skArc(sketch, "E28.1.0.9", {"start": v(141.28, -12.16) * mm, "mid": v(143.4, -11.28) * mm, "end": v(144.28, -9.16) * mm});
            skLineSegment(sketch, "E28.1.0.10", {"start": v(144.28, 253.14) * mm, "end": v(144.28, -9.16) * mm});
            skLineSegment(sketch, "E28.1.0.11", {"start": v(151.87, 253.14) * mm, "end": v(149.78, 253.14) * mm});
            skLineSegment(sketch, "E28.2.0.0", {"start": v(122.03, -21.23) * mm, "end": v(119.03, -21.23) * mm});
            skLineSegment(sketch, "E28.2.0.2", {"start": v(119.03, -21.23) * mm, "end": v(119.03, -18.23) * mm});
            skLineSegment(sketch, "E28.2.0.3", {"start": v(107.44, -18.23) * mm, "end": v(119.03, -18.23) * mm});
            skLineSegment(sketch, "E28.2.0.4", {"start": v(107.44, -21.23) * mm, "end": v(107.44, -18.23) * mm});
            skLineSegment(sketch, "E28.2.0.5", {"start": v(104.44, -21.23) * mm, "end": v(107.44, -21.23) * mm});
            skLineSegment(sketch, "E28.2.0.6", {"start": v(104.44, -18.23) * mm, "end": v(104.44, -21.23) * mm});
            skLineSegment(sketch, "E28.2.0.7", {"start": v(104.44, -12.16) * mm, "end": v(104.44, -18.23) * mm});
            skLineSegment(sketch, "E28.2.0.8", {"start": v(111.44, -12.16) * mm, "end": v(104.44, -12.16) * mm});
            skArc(sketch, "E28.2.0.9", {"start": v(111.44, -12.16) * mm, "mid": v(113.56, -11.28) * mm, "end": v(114.44, -9.16) * mm});
            skLineSegment(sketch, "E28.2.0.10", {"start": v(114.44, 253.14) * mm, "end": v(114.44, -9.16) * mm});
            skLineSegment(sketch, "E28.2.0.11", {"start": v(122.03, 253.14) * mm, "end": v(119.94, 253.14) * mm});
            skLineSegment(sketch, "E28.3.0.0", {"start": v(92.2, -21.23) * mm, "end": v(89.2, -21.23) * mm});
            skLineSegment(sketch, "E28.3.0.2", {"start": v(89.2, -21.23) * mm, "end": v(89.2, -18.23) * mm});
            skLineSegment(sketch, "E28.3.0.3", {"start": v(77.6, -18.23) * mm, "end": v(89.2, -18.23) * mm});
            skLineSegment(sketch, "E28.3.0.4", {"start": v(77.6, -21.23) * mm, "end": v(77.6, -18.23) * mm});
            skLineSegment(sketch, "E28.3.0.5", {"start": v(74.6, -21.23) * mm, "end": v(77.6, -21.23) * mm});
            skLineSegment(sketch, "E28.3.0.6", {"start": v(74.6, -18.23) * mm, "end": v(74.6, -21.23) * mm});
            skLineSegment(sketch, "E28.3.0.7", {"start": v(74.6, -12.16) * mm, "end": v(74.6, -18.23) * mm});
            skLineSegment(sketch, "E28.3.0.8", {"start": v(81.6, -12.16) * mm, "end": v(74.6, -12.16) * mm});
            skArc(sketch, "E28.3.0.9", {"start": v(81.6, -12.16) * mm, "mid": v(83.72, -11.28) * mm, "end": v(84.6, -9.16) * mm});
            skLineSegment(sketch, "E28.3.0.10", {"start": v(84.6, 253.14) * mm, "end": v(84.6, -9.16) * mm});
            skLineSegment(sketch, "E28.3.0.11", {"start": v(92.2, 253.14) * mm, "end": v(90.1, 253.14) * mm});
            skLineSegment(sketch, "E28.4.0.0", {"start": v(62.35, -21.23) * mm, "end": v(59.35, -21.23) * mm});
            skLineSegment(sketch, "E28.4.0.2", {"start": v(59.35, -21.23) * mm, "end": v(59.35, -18.23) * mm});
            skLineSegment(sketch, "E28.4.0.3", {"start": v(47.76, -18.23) * mm, "end": v(59.35, -18.23) * mm});
            skLineSegment(sketch, "E28.4.0.4", {"start": v(47.76, -21.23) * mm, "end": v(47.76, -18.23) * mm});
            skLineSegment(sketch, "E28.4.0.5", {"start": v(44.76, -21.23) * mm, "end": v(47.76, -21.23) * mm});
            skLineSegment(sketch, "E28.4.0.6", {"start": v(44.76, -18.23) * mm, "end": v(44.76, -21.23) * mm});
            skLineSegment(sketch, "E28.4.0.7", {"start": v(44.76, -12.16) * mm, "end": v(44.76, -18.23) * mm});
            skLineSegment(sketch, "E28.4.0.8", {"start": v(51.76, -12.16) * mm, "end": v(44.76, -12.16) * mm});
            skArc(sketch, "E28.4.0.9", {"start": v(51.76, -12.16) * mm, "mid": v(53.88, -11.28) * mm, "end": v(54.76, -9.16) * mm});
            skLineSegment(sketch, "E28.4.0.10", {"start": v(54.76, 253.14) * mm, "end": v(54.76, -9.16) * mm});
            skLineSegment(sketch, "E28.4.0.11", {"start": v(62.35, 253.14) * mm, "end": v(60.26, 253.14) * mm});
            skLineSegment(sketch, "E28.5.0.0", {"start": v(32.51, -21.23) * mm, "end": v(29.51, -21.23) * mm});
            skLineSegment(sketch, "E28.5.0.2", {"start": v(29.51, -21.23) * mm, "end": v(29.51, -18.23) * mm});
            skLineSegment(sketch, "E28.5.0.3", {"start": v(17.92, -18.23) * mm, "end": v(29.51, -18.23) * mm});
            skLineSegment(sketch, "E28.5.0.4", {"start": v(17.92, -21.23) * mm, "end": v(17.92, -18.23) * mm});
            skLineSegment(sketch, "E28.5.0.5", {"start": v(14.92, -21.23) * mm, "end": v(17.92, -21.23) * mm});
            skLineSegment(sketch, "E28.5.0.6", {"start": v(14.92, -18.23) * mm, "end": v(14.92, -21.23) * mm});
            skLineSegment(sketch, "E28.5.0.7", {"start": v(14.92, -12.16) * mm, "end": v(14.92, -18.23) * mm});
            skLineSegment(sketch, "E28.5.0.8", {"start": v(21.92, -12.16) * mm, "end": v(14.92, -12.16) * mm});
            skArc(sketch, "E28.5.0.9", {"start": v(21.92, -12.16) * mm, "mid": v(24.04, -11.28) * mm, "end": v(24.92, -9.16) * mm});
            skLineSegment(sketch, "E28.5.0.10", {"start": v(24.92, 253.14) * mm, "end": v(24.92, -9.16) * mm});
            skLineSegment(sketch, "E28.5.0.11", {"start": v(32.51, 253.14) * mm, "end": v(30.42, 253.14) * mm});
            skLineSegment(sketch, "E28.6.0.0", {"start": v(2.67, -21.23) * mm, "end": v(-0.33, -21.23) * mm});
            skLineSegment(sketch, "E28.6.0.2", {"start": v(-0.33, -21.23) * mm, "end": v(-0.33, -18.23) * mm});
            skLineSegment(sketch, "E28.6.0.3", {"start": v(-11.92, -18.23) * mm, "end": v(-0.33, -18.23) * mm});
            skLineSegment(sketch, "E28.6.0.4", {"start": v(-11.92, -21.23) * mm, "end": v(-11.92, -18.23) * mm});
            skLineSegment(sketch, "E28.6.0.5", {"start": v(-14.92, -21.23) * mm, "end": v(-11.92, -21.23) * mm});
            skLineSegment(sketch, "E28.6.0.6", {"start": v(-14.92, -18.23) * mm, "end": v(-14.92, -21.23) * mm});
            skLineSegment(sketch, "E28.6.0.7", {"start": v(-14.92, -12.16) * mm, "end": v(-14.92, -18.23) * mm});
            skLineSegment(sketch, "E28.6.0.8", {"start": v(-7.92, -12.16) * mm, "end": v(-14.92, -12.16) * mm});
            skArc(sketch, "E28.6.0.9", {"start": v(-7.92, -12.16) * mm, "mid": v(-5.8, -11.28) * mm, "end": v(-4.92, -9.16) * mm});
            skLineSegment(sketch, "E28.6.0.10", {"start": v(-4.92, 253.14) * mm, "end": v(-4.92, -9.16) * mm});
            skLineSegment(sketch, "E28.6.0.11", {"start": v(2.67, 253.14) * mm, "end": v(0.58, 253.14) * mm});
            skLineSegment(sketch, "E28.7.0.0", {"start": v(-27.17, -21.23) * mm, "end": v(-30.17, -21.23) * mm});
            skLineSegment(sketch, "E28.7.0.2", {"start": v(-30.17, -21.23) * mm, "end": v(-30.17, -18.23) * mm});
            skLineSegment(sketch, "E28.7.0.3", {"start": v(-41.76, -18.23) * mm, "end": v(-30.17, -18.23) * mm});
            skLineSegment(sketch, "E28.7.0.4", {"start": v(-41.76, -21.23) * mm, "end": v(-41.76, -18.23) * mm});
            skLineSegment(sketch, "E28.7.0.5", {"start": v(-44.76, -21.23) * mm, "end": v(-41.76, -21.23) * mm});
            skLineSegment(sketch, "E28.7.0.8", {"start": v(-37.76, -12.16) * mm, "end": v(-44.76, -12.16) * mm});
            skArc(sketch, "E28.7.0.9", {"start": v(-37.76, -12.16) * mm, "mid": v(-35.64, -11.28) * mm, "end": v(-34.76, -9.16) * mm});
            skLineSegment(sketch, "E28.7.0.10", {"start": v(-34.76, 253.14) * mm, "end": v(-34.76, -9.16) * mm});
            skLineSegment(sketch, "E28.7.0.11", {"start": v(-27.17, 253.14) * mm, "end": v(-29.26, 253.14) * mm});
            skLineSegment(sketch, "E28.direction1", {"start": v(178.71, -21.23) * mm, "end": v(148.87, -21.23) * mm, "construction": true});
            skPoint(sketch, "E29.orphan", {"position": v(34.51, 253.14) * mm});
            skPoint(sketch, "E30.orphan", {"position": v(64.35, 253.14) * mm});
            skPoint(sketch, "E31.orphan", {"position": v(94.2, 253.14) * mm});
            skPoint(sketch, "E32.orphan", {"position": v(124.03, 253.14) * mm});
            skPoint(sketch, "E33.orphan", {"position": v(153.87, 253.14) * mm});
            skLineSegment(sketch, "E34", {"start": v(176.62, 253.14) * mm, "end": v(174.12, 253.14) * mm});
            skLineSegment(sketch, "E35.top", {"start": v(179.62, 256.14) * mm, "end": v(176.62, 256.14) * mm});
            skLineSegment(sketch, "E35.left", {"start": v(179.62, 253.14) * mm, "end": v(179.62, 256.14) * mm});
            skLineSegment(sketch, "E35.right", {"start": v(176.62, 253.14) * mm, "end": v(176.62, 256.14) * mm});
            skLineSegment(sketch, "E36.1.0.0", {"start": v(149.78, 253.14) * mm, "end": v(149.78, 256.14) * mm});
            skLineSegment(sketch, "E36.1.0.1", {"start": v(149.78, 256.14) * mm, "end": v(146.78, 256.14) * mm});
            skLineSegment(sketch, "E36.1.0.2", {"start": v(146.78, 253.14) * mm, "end": v(146.78, 256.14) * mm});
            skLineSegment(sketch, "E36.2.0.0", {"start": v(119.94, 253.14) * mm, "end": v(119.94, 256.14) * mm});
            skLineSegment(sketch, "E36.2.0.1", {"start": v(119.94, 256.14) * mm, "end": v(116.94, 256.14) * mm});
            skLineSegment(sketch, "E36.2.0.2", {"start": v(116.94, 253.14) * mm, "end": v(116.94, 256.14) * mm});
            skLineSegment(sketch, "E36.3.0.0", {"start": v(90.1, 253.14) * mm, "end": v(90.1, 256.14) * mm});
            skLineSegment(sketch, "E36.3.0.1", {"start": v(90.1, 256.14) * mm, "end": v(87.1, 256.14) * mm});
            skLineSegment(sketch, "E36.3.0.2", {"start": v(87.1, 253.14) * mm, "end": v(87.1, 256.14) * mm});
            skLineSegment(sketch, "E36.4.0.0", {"start": v(60.26, 253.14) * mm, "end": v(60.26, 256.14) * mm});
            skLineSegment(sketch, "E36.4.0.1", {"start": v(60.26, 256.14) * mm, "end": v(57.26, 256.14) * mm});
            skLineSegment(sketch, "E36.4.0.2", {"start": v(57.26, 253.14) * mm, "end": v(57.26, 256.14) * mm});
            skLineSegment(sketch, "E36.5.0.0", {"start": v(30.42, 253.14) * mm, "end": v(30.42, 256.14) * mm});
            skLineSegment(sketch, "E36.5.0.1", {"start": v(30.42, 256.14) * mm, "end": v(27.42, 256.14) * mm});
            skLineSegment(sketch, "E36.5.0.2", {"start": v(27.42, 253.14) * mm, "end": v(27.42, 256.14) * mm});
            skLineSegment(sketch, "E36.6.0.0", {"start": v(0.58, 253.14) * mm, "end": v(0.58, 256.14) * mm});
            skLineSegment(sketch, "E36.6.0.1", {"start": v(0.58, 256.14) * mm, "end": v(-2.42, 256.14) * mm});
            skLineSegment(sketch, "E36.6.0.2", {"start": v(-2.42, 253.14) * mm, "end": v(-2.42, 256.14) * mm});
            skLineSegment(sketch, "E36.7.0.0", {"start": v(-29.26, 253.14) * mm, "end": v(-29.26, 256.14) * mm});
            skLineSegment(sketch, "E36.7.0.1", {"start": v(-29.26, 256.14) * mm, "end": v(-32.26, 256.14) * mm});
            skLineSegment(sketch, "E36.7.0.2", {"start": v(-32.26, 253.14) * mm, "end": v(-32.26, 256.14) * mm});
            skLineSegment(sketch, "E36.direction1", {"start": v(179.62, 253.14) * mm, "end": v(149.78, 253.14) * mm, "construction": true});
            skLineSegment(sketch, "E37.trimOffspring", {"start": v(146.78, 253.14) * mm, "end": v(144.28, 253.14) * mm});
            skLineSegment(sketch, "E38.trimOffspring", {"start": v(116.94, 253.14) * mm, "end": v(114.44, 253.14) * mm});
            skLineSegment(sketch, "E39.trimOffspring", {"start": v(87.1, 253.14) * mm, "end": v(84.6, 253.14) * mm});
            skLineSegment(sketch, "E40.trimOffspring", {"start": v(57.26, 253.14) * mm, "end": v(54.76, 253.14) * mm});
            skLineSegment(sketch, "E41.trimOffspring", {"start": v(27.42, 253.14) * mm, "end": v(24.92, 253.14) * mm});
            skLineSegment(sketch, "E42.trimOffspring", {"start": v(-2.42, 253.14) * mm, "end": v(-4.92, 253.14) * mm});
            skLineSegment(sketch, "E43.trimOffspring", {"start": v(-32.26, 253.14) * mm, "end": v(-34.76, 253.14) * mm});
            skLineSegment(sketch, "E44", {"start": v(151.87, 2.02) * mm, "end": v(151.87, -21.23) * mm});
            skLineSegment(sketch, "E45", {"start": v(122.03, 0.4) * mm, "end": v(122.03, -21.23) * mm});
            skLineSegment(sketch, "E46", {"start": v(92.2, -1.23) * mm, "end": v(92.2, -21.23) * mm});
            skLineSegment(sketch, "E47", {"start": v(62.35, -2.86) * mm, "end": v(62.35, -21.23) * mm});
            skLineSegment(sketch, "E48", {"start": v(32.51, -4.48) * mm, "end": v(32.51, -21.23) * mm});
            skLineSegment(sketch, "E49", {"start": v(2.67, -6.1) * mm, "end": v(2.67, -21.23) * mm});
            skLineSegment(sketch, "E50", {"start": v(-27.17, -7.73) * mm, "end": v(-27.17, -21.23) * mm});
            skLineSegment(sketch, "E51", {"start": v(-44.76, -12.16) * mm, "end": v(-44.76, -21.23) * mm});
            skLineSegment(sketch, "E52", {"start": v(-27.26, 241.77) * mm, "end": v(-25.17, 241.77) * mm});
            skText(sketch, "E53", { "text": "1", "fontName": "OpenSans-Bold.ttf"});
            skText(sketch, "E54", { "text": "2", "fontName": "OpenSans-Bold.ttf"});
            skText(sketch, "E55", { "text": "3", "fontName": "OpenSans-Bold.ttf"});
            skText(sketch, "E56", { "text": "4", "fontName": "OpenSans-Regular.ttf"});
            skText(sketch, "E57", { "text": "5", "fontName": "OpenSans-Bold.ttf"});
            skText(sketch, "E58", { "text": "6", "fontName": "OpenSans-Bold.ttf"});
            skText(sketch, "E59", { "text": "7", "fontName": "OpenSans-Bold.ttf"});
            skText(sketch, "E60", { "text": "8", "fontName": "OpenSans-Bold.ttf"});
            const initialGuessF1  = {"E53": [-0.03306, -0.01492, 1, 0, 0.00464], "E54": [-0.0038, -0.0154, 1, 0, 0.00496], "E55": [0.02564, -0.01501, 1, 0, 0.005], "E56": [0.05553, -0.01466, 1, 0, 0.00506], "E57": [0.08577, -0.01514, 1, 0, 0.00496], "E58": [0.11579, -0.01498, 1, 0, 0.00467], "E59": [0.14587, -0.0152, 1, 0, 0.0048], "E60": [0.17538, -0.01583, 1, 0, 0.00513]};
            skSetInitialGuess(sketch, initialGuessF1);
            skSolve(sketch);
        }
        {
            var Q0;
            Q0=qCreatedBy(makeId("Top.planeOp"),FACE);
            var sketch = newSketch(context, id + "F2", { "sketchPlane" : qUnion([Q0])});
            skCircle(sketch, "E61", {"center": v(0, 0) * mm, "radius": 38 * mm});
            skCircle(sketch, "E62", {"center": v(0, 0) * mm, "radius": 17 * mm});
            skLineSegment(sketch, "E63.bottom", {"start": v(35.51, -1.5) * mm, "end": v(32.51, -1.5) * mm});
            skLineSegment(sketch, "E63.top", {"start": v(35.51, 1.5) * mm, "end": v(32.51, 1.5) * mm});
            skLineSegment(sketch, "E63.left", {"start": v(35.51, -1.5) * mm, "end": v(35.51, 1.5) * mm});
            skLineSegment(sketch, "E63.right", {"start": v(32.51, -1.5) * mm, "end": v(32.51, 1.5) * mm});
            skPoint(sketch, "E63.middle", {"position": v(31.01, 0) * mm});
            skLineSegment(sketch, "E64.bottom", {"start": v(20.92, -1.5) * mm, "end": v(17.92, -1.5) * mm});
            skLineSegment(sketch, "E64.top", {"start": v(20.92, 1.5) * mm, "end": v(17.92, 1.5) * mm});
            skLineSegment(sketch, "E64.left", {"start": v(20.92, -1.5) * mm, "end": v(20.92, 1.5) * mm});
            skLineSegment(sketch, "E64.right", {"start": v(17.92, -1.5) * mm, "end": v(17.92, 1.5) * mm});
            skPoint(sketch, "E64.middle", {"position": v(16.42, 0) * mm});
            skLineSegment(sketch, "E65.1.0", {"start": v(13.73, 15.85) * mm, "end": v(11.6, 13.73) * mm});
            skLineSegment(sketch, "E65.1.1", {"start": v(15.85, 13.73) * mm, "end": v(13.73, 11.6) * mm});
            skLineSegment(sketch, "E65.1.2", {"start": v(13.73, 11.6) * mm, "end": v(11.6, 13.73) * mm});
            skLineSegment(sketch, "E65.1.3", {"start": v(15.85, 13.73) * mm, "end": v(13.73, 15.85) * mm});
            skLineSegment(sketch, "E65.1.4", {"start": v(24.05, 21.93) * mm, "end": v(21.93, 24.05) * mm});
            skLineSegment(sketch, "E65.1.5", {"start": v(24.05, 26.17) * mm, "end": v(21.93, 24.05) * mm});
            skLineSegment(sketch, "E65.1.6", {"start": v(26.17, 24.05) * mm, "end": v(24.05, 26.17) * mm});
            skLineSegment(sketch, "E65.1.7", {"start": v(26.17, 24.05) * mm, "end": v(24.05, 21.93) * mm});
            skLineSegment(sketch, "E65.2.0", {"start": v(-1.5, 20.92) * mm, "end": v(-1.5, 17.92) * mm});
            skLineSegment(sketch, "E65.2.1", {"start": v(1.5, 20.92) * mm, "end": v(1.5, 17.92) * mm});
            skLineSegment(sketch, "E65.2.2", {"start": v(1.5, 17.92) * mm, "end": v(-1.5, 17.92) * mm});
            skLineSegment(sketch, "E65.2.3", {"start": v(1.5, 20.92) * mm, "end": v(-1.5, 20.92) * mm});
            skLineSegment(sketch, "E65.2.4", {"start": v(1.5, 32.51) * mm, "end": v(-1.5, 32.51) * mm});
            skLineSegment(sketch, "E65.2.5", {"start": v(-1.5, 35.51) * mm, "end": v(-1.5, 32.51) * mm});
            skLineSegment(sketch, "E65.2.6", {"start": v(1.5, 35.51) * mm, "end": v(-1.5, 35.51) * mm});
            skLineSegment(sketch, "E65.2.7", {"start": v(1.5, 35.51) * mm, "end": v(1.5, 32.51) * mm});
            skLineSegment(sketch, "E65.3.0", {"start": v(-15.85, 13.73) * mm, "end": v(-13.73, 11.6) * mm});
            skLineSegment(sketch, "E65.3.1", {"start": v(-13.73, 15.85) * mm, "end": v(-11.6, 13.73) * mm});
            skLineSegment(sketch, "E65.3.2", {"start": v(-11.6, 13.73) * mm, "end": v(-13.73, 11.6) * mm});
            skLineSegment(sketch, "E65.3.3", {"start": v(-13.73, 15.85) * mm, "end": v(-15.85, 13.73) * mm});
            skLineSegment(sketch, "E65.3.4", {"start": v(-21.93, 24.05) * mm, "end": v(-24.05, 21.93) * mm});
            skLineSegment(sketch, "E65.3.5", {"start": v(-26.17, 24.05) * mm, "end": v(-24.05, 21.93) * mm});
            skLineSegment(sketch, "E65.3.6", {"start": v(-24.05, 26.17) * mm, "end": v(-26.17, 24.05) * mm});
            skLineSegment(sketch, "E65.3.7", {"start": v(-24.05, 26.17) * mm, "end": v(-21.93, 24.05) * mm});
            skLineSegment(sketch, "E65.4.0", {"start": v(-20.92, -1.5) * mm, "end": v(-17.92, -1.5) * mm});
            skLineSegment(sketch, "E65.4.1", {"start": v(-20.92, 1.5) * mm, "end": v(-17.92, 1.5) * mm});
            skLineSegment(sketch, "E65.4.2", {"start": v(-17.92, 1.5) * mm, "end": v(-17.92, -1.5) * mm});
            skLineSegment(sketch, "E65.4.3", {"start": v(-20.92, 1.5) * mm, "end": v(-20.92, -1.5) * mm});
            skLineSegment(sketch, "E65.4.4", {"start": v(-32.51, 1.5) * mm, "end": v(-32.51, -1.5) * mm});
            skLineSegment(sketch, "E65.4.5", {"start": v(-35.51, -1.5) * mm, "end": v(-32.51, -1.5) * mm});
            skLineSegment(sketch, "E65.4.6", {"start": v(-35.51, 1.5) * mm, "end": v(-35.51, -1.5) * mm});
            skLineSegment(sketch, "E65.4.7", {"start": v(-35.51, 1.5) * mm, "end": v(-32.51, 1.5) * mm});
            skLineSegment(sketch, "E65.5.0", {"start": v(-13.73, -15.85) * mm, "end": v(-11.6, -13.73) * mm});
            skLineSegment(sketch, "E65.5.1", {"start": v(-15.85, -13.73) * mm, "end": v(-13.73, -11.6) * mm});
            skLineSegment(sketch, "E65.5.2", {"start": v(-13.73, -11.6) * mm, "end": v(-11.6, -13.73) * mm});
            skLineSegment(sketch, "E65.5.3", {"start": v(-15.85, -13.73) * mm, "end": v(-13.73, -15.85) * mm});
            skLineSegment(sketch, "E65.5.4", {"start": v(-24.05, -21.93) * mm, "end": v(-21.93, -24.05) * mm});
            skLineSegment(sketch, "E65.5.5", {"start": v(-24.05, -26.17) * mm, "end": v(-21.93, -24.05) * mm});
            skLineSegment(sketch, "E65.5.6", {"start": v(-26.17, -24.05) * mm, "end": v(-24.05, -26.17) * mm});
            skLineSegment(sketch, "E65.5.7", {"start": v(-26.17, -24.05) * mm, "end": v(-24.05, -21.93) * mm});
            skLineSegment(sketch, "E65.6.0", {"start": v(1.5, -20.92) * mm, "end": v(1.5, -17.92) * mm});
            skLineSegment(sketch, "E65.6.1", {"start": v(-1.5, -20.92) * mm, "end": v(-1.5, -17.92) * mm});
            skLineSegment(sketch, "E65.6.2", {"start": v(-1.5, -17.92) * mm, "end": v(1.5, -17.92) * mm});
            skLineSegment(sketch, "E65.6.3", {"start": v(-1.5, -20.92) * mm, "end": v(1.5, -20.92) * mm});
            skLineSegment(sketch, "E65.6.4", {"start": v(-1.5, -32.51) * mm, "end": v(1.5, -32.51) * mm});
            skLineSegment(sketch, "E65.6.5", {"start": v(1.5, -35.51) * mm, "end": v(1.5, -32.51) * mm});
            skLineSegment(sketch, "E65.6.6", {"start": v(-1.5, -35.51) * mm, "end": v(1.5, -35.51) * mm});
            skLineSegment(sketch, "E65.6.7", {"start": v(-1.5, -35.51) * mm, "end": v(-1.5, -32.51) * mm});
            skLineSegment(sketch, "E65.7.0", {"start": v(15.85, -13.73) * mm, "end": v(13.73, -11.6) * mm});
            skLineSegment(sketch, "E65.7.1", {"start": v(13.73, -15.85) * mm, "end": v(11.6, -13.73) * mm});
            skLineSegment(sketch, "E65.7.2", {"start": v(11.6, -13.73) * mm, "end": v(13.73, -11.6) * mm});
            skLineSegment(sketch, "E65.7.3", {"start": v(13.73, -15.85) * mm, "end": v(15.85, -13.73) * mm});
            skLineSegment(sketch, "E65.7.4", {"start": v(21.93, -24.05) * mm, "end": v(24.05, -21.93) * mm});
            skLineSegment(sketch, "E65.7.5", {"start": v(26.17, -24.05) * mm, "end": v(24.05, -21.93) * mm});
            skLineSegment(sketch, "E65.7.6", {"start": v(24.05, -26.17) * mm, "end": v(26.17, -24.05) * mm});
            skLineSegment(sketch, "E65.7.7", {"start": v(24.05, -26.17) * mm, "end": v(21.93, -24.05) * mm});
            skSolve(sketch);
        }
        {
            var Q0;
            Q0=makeQuery(id+"F2.imprint","IMPRINT",FACE,{"disambiguationData":[TD([[makeQuery(id+"F2.imprint","IMPRINT",EDGE,{"derivedFrom":sQuery(id+"F2.wireOp",EDGE,"E61")}),1.0]])]});
            extrude(context, id + "F3", {"entities" : qUnion([Q0]), "depth" : (getVariable(context, 'thickness')) * mm, "offsetDistance" : 25 * mm});
        }
        {
            var Q0;
            Q0=makeQuery(id+"F3.opExtrude","CAP_FACE",FACE,{"disambiguationData":[OSD([sQuery(id+"F2.wireOp",EDGE,"E61"),sQuery(id+"F2.wireOp",EDGE,"E62"),sQuery(id+"F2.wireOp",EDGE,"E63.bottom"),sQuery(id+"F2.wireOp",EDGE,"E63.top"),sQuery(id+"F2.wireOp",EDGE,"E63.left"),sQuery(id+"F2.wireOp",EDGE,"E63.right"),sQuery(id+"F2.wireOp",EDGE,"E64.bottom"),sQuery(id+"F2.wireOp",EDGE,"E64.top"),sQuery(id+"F2.wireOp",EDGE,"E64.left"),sQuery(id+"F2.wireOp",EDGE,"E64.right"),sQuery(id+"F2.wireOp",EDGE,"E65.1.0"),sQuery(id+"F2.wireOp",EDGE,"E65.1.1"),sQuery(id+"F2.wireOp",EDGE,"E65.1.2"),sQuery(id+"F2.wireOp",EDGE,"E65.1.3"),sQuery(id+"F2.wireOp",EDGE,"E65.1.4"),sQuery(id+"F2.wireOp",EDGE,"E65.1.5"),sQuery(id+"F2.wireOp",EDGE,"E65.1.6"),sQuery(id+"F2.wireOp",EDGE,"E65.1.7"),sQuery(id+"F2.wireOp",EDGE,"E65.2.0"),sQuery(id+"F2.wireOp",EDGE,"E65.2.1"),sQuery(id+"F2.wireOp",EDGE,"E65.2.2"),sQuery(id+"F2.wireOp",EDGE,"E65.2.3"),sQuery(id+"F2.wireOp",EDGE,"E65.2.4"),sQuery(id+"F2.wireOp",EDGE,"E65.2.5"),sQuery(id+"F2.wireOp",EDGE,"E65.2.6"),sQuery(id+"F2.wireOp",EDGE,"E65.2.7"),sQuery(id+"F2.wireOp",EDGE,"E65.3.0"),sQuery(id+"F2.wireOp",EDGE,"E65.3.1"),sQuery(id+"F2.wireOp",EDGE,"E65.3.2"),sQuery(id+"F2.wireOp",EDGE,"E65.3.3"),sQuery(id+"F2.wireOp",EDGE,"E65.3.4"),sQuery(id+"F2.wireOp",EDGE,"E65.3.5"),sQuery(id+"F2.wireOp",EDGE,"E65.3.6"),sQuery(id+"F2.wireOp",EDGE,"E65.3.7"),sQuery(id+"F2.wireOp",EDGE,"E65.4.0"),sQuery(id+"F2.wireOp",EDGE,"E65.4.1"),sQuery(id+"F2.wireOp",EDGE,"E65.4.2"),sQuery(id+"F2.wireOp",EDGE,"E65.4.3"),sQuery(id+"F2.wireOp",EDGE,"E65.4.4"),sQuery(id+"F2.wireOp",EDGE,"E65.4.5"),sQuery(id+"F2.wireOp",EDGE,"E65.4.6"),sQuery(id+"F2.wireOp",EDGE,"E65.4.7"),sQuery(id+"F2.wireOp",EDGE,"E65.5.0"),sQuery(id+"F2.wireOp",EDGE,"E65.5.1"),sQuery(id+"F2.wireOp",EDGE,"E65.5.2"),sQuery(id+"F2.wireOp",EDGE,"E65.5.3"),sQuery(id+"F2.wireOp",EDGE,"E65.5.4"),sQuery(id+"F2.wireOp",EDGE,"E65.5.5"),sQuery(id+"F2.wireOp",EDGE,"E65.5.6"),sQuery(id+"F2.wireOp",EDGE,"E65.5.7"),sQuery(id+"F2.wireOp",EDGE,"E65.6.0"),sQuery(id+"F2.wireOp",EDGE,"E65.6.1"),sQuery(id+"F2.wireOp",EDGE,"E65.6.2"),sQuery(id+"F2.wireOp",EDGE,"E65.6.3"),sQuery(id+"F2.wireOp",EDGE,"E65.6.4"),sQuery(id+"F2.wireOp",EDGE,"E65.6.5"),sQuery(id+"F2.wireOp",EDGE,"E65.6.6"),sQuery(id+"F2.wireOp",EDGE,"E65.6.7"),sQuery(id+"F2.wireOp",EDGE,"E65.7.0"),sQuery(id+"F2.wireOp",EDGE,"E65.7.1"),sQuery(id+"F2.wireOp",EDGE,"E65.7.2"),sQuery(id+"F2.wireOp",EDGE,"E65.7.3"),sQuery(id+"F2.wireOp",EDGE,"E65.7.4"),sQuery(id+"F2.wireOp",EDGE,"E65.7.5"),sQuery(id+"F2.wireOp",EDGE,"E65.7.6"),sQuery(id+"F2.wireOp",EDGE,"E65.7.7")])],"isStart":false});
            var sketch = newSketch(context, id + "F4", { "sketchPlane" : qUnion([Q0])});
            skCircle(sketch, "E66", {"center": v(0, 0) * mm, "radius": 38 * mm});
            skCircle(sketch, "E67", {"center": v(0, 0) * mm, "radius": 25 * mm});
            skLineSegment(sketch, "E68.bottom", {"start": v(30.2, 1.5) * mm, "end": v(33.6, 1.5) * mm});
            skLineSegment(sketch, "E68.top", {"start": v(30.2, -1.5) * mm, "end": v(33.6, -1.5) * mm});
            skLineSegment(sketch, "E68.left", {"start": v(30.2, 1.5) * mm, "end": v(30.2, -1.5) * mm});
            skLineSegment(sketch, "E68.right", {"start": v(33.6, 1.5) * mm, "end": v(33.6, -1.5) * mm});
            skLineSegment(sketch, "E69.1.0", {"start": v(20.3, 22.4) * mm, "end": v(22.7, 24.81) * mm});
            skLineSegment(sketch, "E69.1.1", {"start": v(20.3, 22.4) * mm, "end": v(22.42, 20.29) * mm});
            skLineSegment(sketch, "E69.1.2", {"start": v(22.42, 20.29) * mm, "end": v(24.83, 22.7) * mm});
            skLineSegment(sketch, "E69.1.3", {"start": v(22.7, 24.81) * mm, "end": v(24.83, 22.7) * mm});
            skLineSegment(sketch, "E69.2.0", {"start": v(-1.5, 30.2) * mm, "end": v(-1.5, 33.6) * mm});
            skLineSegment(sketch, "E69.2.1", {"start": v(-1.5, 30.2) * mm, "end": v(1.5, 30.2) * mm});
            skLineSegment(sketch, "E69.2.2", {"start": v(1.5, 30.2) * mm, "end": v(1.5, 33.6) * mm});
            skLineSegment(sketch, "E69.2.3", {"start": v(-1.5, 33.6) * mm, "end": v(1.5, 33.6) * mm});
            skLineSegment(sketch, "E69.3.0", {"start": v(-22.4, 20.3) * mm, "end": v(-24.81, 22.7) * mm});
            skLineSegment(sketch, "E69.3.1", {"start": v(-22.4, 20.3) * mm, "end": v(-20.29, 22.42) * mm});
            skLineSegment(sketch, "E69.3.2", {"start": v(-20.29, 22.42) * mm, "end": v(-22.7, 24.83) * mm});
            skLineSegment(sketch, "E69.3.3", {"start": v(-24.81, 22.7) * mm, "end": v(-22.7, 24.83) * mm});
            skLineSegment(sketch, "E69.4.0", {"start": v(-30.2, -1.5) * mm, "end": v(-33.6, -1.5) * mm});
            skLineSegment(sketch, "E69.4.1", {"start": v(-30.2, -1.5) * mm, "end": v(-30.2, 1.5) * mm});
            skLineSegment(sketch, "E69.4.2", {"start": v(-30.2, 1.5) * mm, "end": v(-33.6, 1.5) * mm});
            skLineSegment(sketch, "E69.4.3", {"start": v(-33.6, -1.5) * mm, "end": v(-33.6, 1.5) * mm});
            skLineSegment(sketch, "E69.5.0", {"start": v(-20.3, -22.4) * mm, "end": v(-22.7, -24.81) * mm});
            skLineSegment(sketch, "E69.5.1", {"start": v(-20.3, -22.4) * mm, "end": v(-22.42, -20.29) * mm});
            skLineSegment(sketch, "E69.5.2", {"start": v(-22.42, -20.29) * mm, "end": v(-24.83, -22.7) * mm});
            skLineSegment(sketch, "E69.5.3", {"start": v(-22.7, -24.81) * mm, "end": v(-24.83, -22.7) * mm});
            skLineSegment(sketch, "E69.6.0", {"start": v(1.5, -30.2) * mm, "end": v(1.5, -33.6) * mm});
            skLineSegment(sketch, "E69.6.1", {"start": v(1.5, -30.2) * mm, "end": v(-1.5, -30.2) * mm});
            skLineSegment(sketch, "E69.6.2", {"start": v(-1.5, -30.2) * mm, "end": v(-1.5, -33.6) * mm});
            skLineSegment(sketch, "E69.6.3", {"start": v(1.5, -33.6) * mm, "end": v(-1.5, -33.6) * mm});
            skLineSegment(sketch, "E69.7.0", {"start": v(22.4, -20.3) * mm, "end": v(24.81, -22.7) * mm});
            skLineSegment(sketch, "E69.7.1", {"start": v(22.4, -20.3) * mm, "end": v(20.29, -22.42) * mm});
            skLineSegment(sketch, "E69.7.2", {"start": v(20.29, -22.42) * mm, "end": v(22.7, -24.83) * mm});
            skLineSegment(sketch, "E69.7.3", {"start": v(24.81, -22.7) * mm, "end": v(22.7, -24.83) * mm});
            skLineSegment(sketch, "E70.bottom", {"start": v(23.5, -17.5) * mm, "end": v(-23.5, -17.5) * mm});
            skLineSegment(sketch, "E70.top", {"start": v(23.5, 17.5) * mm, "end": v(-23.5, 17.5) * mm});
            skLineSegment(sketch, "E70.left", {"start": v(25.5, -15.5) * mm, "end": v(25.5, 15.5) * mm});
            skLineSegment(sketch, "E70.right", {"start": v(-25.5, -15.5) * mm, "end": v(-25.5, 15.5) * mm});
            skPoint(sketch, "E71.visualSharp", {"position": v(-25.5, 17.5) * mm});
            skArc(sketch, "E71.filletArc", {"start": v(-23.5, 17.5) * mm, "mid": v(-24.91, 16.91) * mm, "end": v(-25.5, 15.5) * mm});
            skPoint(sketch, "E72.visualSharp", {"position": v(25.5, -17.5) * mm});
            skArc(sketch, "E72.filletArc", {"start": v(23.5, -17.5) * mm, "mid": v(24.91, -16.91) * mm, "end": v(25.5, -15.5) * mm});
            skPoint(sketch, "E73.visualSharp", {"position": v(25.5, 17.5) * mm});
            skArc(sketch, "E73.filletArc", {"start": v(25.5, 15.5) * mm, "mid": v(24.91, 16.91) * mm, "end": v(23.5, 17.5) * mm});
            skPoint(sketch, "E74.visualSharp", {"position": v(-25.5, -17.5) * mm});
            skArc(sketch, "E74.filletArc", {"start": v(-25.5, -15.5) * mm, "mid": v(-24.91, -16.91) * mm, "end": v(-23.5, -17.5) * mm});
            skSolve(sketch);
        }
        {
            var Q0;
            Q0=makeQuery(id+"F4.imprint","IMPRINT",FACE,{"disambiguationData":[TD([[makeQuery(id+"F4.imprint","IMPRINT",EDGE,{"derivedFrom":sQuery(id+"F4.wireOp",EDGE,"E66")}),1.0]])]});
            var Q1;
            {var subQ0=makeQuery(id+"F3.opExtrude","CAP_EDGE",EDGE,{"disambiguationData":[OSD([sQuery(id+"F2.wireOp",EDGE,"E65.7.5")])],"isStart":false});Q1=makeQuery(id+"F4.imprint","IMPRINT",FACE,{"disambiguationData":[TD([[makeQuery(id+"F4.imprint","IMPRINT",EDGE,{"derivedFrom":subQ0}),1.0]])]});}
            var Q2;
            {var subQ1=makeQuery(id+"F3.opExtrude","CAP_EDGE",EDGE,{"disambiguationData":[OSD([sQuery(id+"F2.wireOp",EDGE,"E63.top")])],"isStart":false});Q2=makeQuery(id+"F4.imprint","IMPRINT",FACE,{"disambiguationData":[TD([[makeQuery(id+"F4.imprint","IMPRINT",EDGE,{"derivedFrom":subQ1}),1.0]])]});}
            var Q3;
            {var subQ0=makeQuery(id+"F3.opExtrude","CAP_EDGE",EDGE,{"disambiguationData":[OSD([sQuery(id+"F2.wireOp",EDGE,"E65.6.5")])],"isStart":false});Q3=makeQuery(id+"F4.imprint","IMPRINT",FACE,{"disambiguationData":[TD([[makeQuery(id+"F4.imprint","IMPRINT",EDGE,{"derivedFrom":subQ0}),1.0]])]});}
            var Q4;
            {var subQ0=makeQuery(id+"F3.opExtrude","CAP_EDGE",EDGE,{"disambiguationData":[OSD([sQuery(id+"F2.wireOp",EDGE,"E65.5.5")])],"isStart":false});Q4=makeQuery(id+"F4.imprint","IMPRINT",FACE,{"disambiguationData":[TD([[makeQuery(id+"F4.imprint","IMPRINT",EDGE,{"derivedFrom":subQ0}),1.0]])]});}
            var Q5;
            {var subQ0=makeQuery(id+"F3.opExtrude","CAP_EDGE",EDGE,{"disambiguationData":[OSD([sQuery(id+"F2.wireOp",EDGE,"E65.4.5")])],"isStart":false});Q5=makeQuery(id+"F4.imprint","IMPRINT",FACE,{"disambiguationData":[TD([[makeQuery(id+"F4.imprint","IMPRINT",EDGE,{"derivedFrom":subQ0}),1.0]])]});}
            var Q6;
            {var subQ0=makeQuery(id+"F3.opExtrude","CAP_EDGE",EDGE,{"disambiguationData":[OSD([sQuery(id+"F2.wireOp",EDGE,"E65.3.5")])],"isStart":false});Q6=makeQuery(id+"F4.imprint","IMPRINT",FACE,{"disambiguationData":[TD([[makeQuery(id+"F4.imprint","IMPRINT",EDGE,{"derivedFrom":subQ0}),1.0]])]});}
            var Q7;
            {var subQ0=makeQuery(id+"F3.opExtrude","CAP_EDGE",EDGE,{"disambiguationData":[OSD([sQuery(id+"F2.wireOp",EDGE,"E65.2.5")])],"isStart":false});Q7=makeQuery(id+"F4.imprint","IMPRINT",FACE,{"disambiguationData":[TD([[makeQuery(id+"F4.imprint","IMPRINT",EDGE,{"derivedFrom":subQ0}),1.0]])]});}
            var Q8;
            {var subQ0=makeQuery(id+"F3.opExtrude","CAP_EDGE",EDGE,{"disambiguationData":[OSD([sQuery(id+"F2.wireOp",EDGE,"E65.1.5")])],"isStart":false});Q8=makeQuery(id+"F4.imprint","IMPRINT",FACE,{"disambiguationData":[TD([[makeQuery(id+"F4.imprint","IMPRINT",EDGE,{"derivedFrom":subQ0}),1.0]])]});}
            extrude(context, id + "F5", {"entities" : qUnion([Q0, Q1, Q2, Q3, Q4, Q5, Q6, Q7, Q8]), "depth" : (getVariable(context, 'thickness')) * mm, "offsetDistance" : 25 * mm});
        }
        {
            var Q0;
            Q0=makeQuery(id+"F5.opExtrude","CAP_FACE",FACE,{"disambiguationData":[OSD([sQuery(id+"F4.wireOp",EDGE,"E66"),sQuery(id+"F4.wireOp",EDGE,"E67"),sQuery(id+"F4.wireOp",EDGE,"E68.bottom"),sQuery(id+"F4.wireOp",EDGE,"E68.top"),sQuery(id+"F4.wireOp",EDGE,"E68.left"),sQuery(id+"F4.wireOp",EDGE,"E68.right"),sQuery(id+"F4.wireOp",EDGE,"E69.1.0"),sQuery(id+"F4.wireOp",EDGE,"E69.1.1"),sQuery(id+"F4.wireOp",EDGE,"E69.1.2"),sQuery(id+"F4.wireOp",EDGE,"E69.1.3"),sQuery(id+"F4.wireOp",EDGE,"E69.2.0"),sQuery(id+"F4.wireOp",EDGE,"E69.2.1"),sQuery(id+"F4.wireOp",EDGE,"E69.2.2"),sQuery(id+"F4.wireOp",EDGE,"E69.2.3"),sQuery(id+"F4.wireOp",EDGE,"E69.3.0"),sQuery(id+"F4.wireOp",EDGE,"E69.3.1"),sQuery(id+"F4.wireOp",EDGE,"E69.3.2"),sQuery(id+"F4.wireOp",EDGE,"E69.3.3"),sQuery(id+"F4.wireOp",EDGE,"E69.4.0"),sQuery(id+"F4.wireOp",EDGE,"E69.4.1"),sQuery(id+"F4.wireOp",EDGE,"E69.4.2"),sQuery(id+"F4.wireOp",EDGE,"E69.4.3"),sQuery(id+"F4.wireOp",EDGE,"E69.5.0"),sQuery(id+"F4.wireOp",EDGE,"E69.5.1"),sQuery(id+"F4.wireOp",EDGE,"E69.5.2"),sQuery(id+"F4.wireOp",EDGE,"E69.5.3"),sQuery(id+"F4.wireOp",EDGE,"E69.6.0"),sQuery(id+"F4.wireOp",EDGE,"E69.6.1"),sQuery(id+"F4.wireOp",EDGE,"E69.6.2"),sQuery(id+"F4.wireOp",EDGE,"E69.6.3"),sQuery(id+"F4.wireOp",EDGE,"E69.7.0"),sQuery(id+"F4.wireOp",EDGE,"E69.7.1"),sQuery(id+"F4.wireOp",EDGE,"E69.7.2"),sQuery(id+"F4.wireOp",EDGE,"E69.7.3"),sQuery(id+"F4.wireOp",EDGE,"E70.bottom"),sQuery(id+"F4.wireOp",EDGE,"E70.top"),sQuery(id+"F4.wireOp",EDGE,"E70.left"),sQuery(id+"F4.wireOp",EDGE,"E70.right"),sQuery(id+"F4.wireOp",EDGE,"E71.filletArc"),sQuery(id+"F4.wireOp",EDGE,"E72.filletArc"),sQuery(id+"F4.wireOp",EDGE,"E73.filletArc"),sQuery(id+"F4.wireOp",EDGE,"E74.filletArc")])],"isStart":false});
            var sketch = newSketch(context, id + "F6", { "sketchPlane" : qUnion([Q0])});
            skCircle(sketch, "E75", {"center": v(0, 0) * mm, "radius": 26 * mm});
            skCircle(sketch, "E76", {"center": v(0, 0) * mm, "radius": 31 * mm});
            skPoint(sketch, "E77.start.orphan", {"position": v(28.36, -1.5) * mm});
            skLineSegment(sketch, "E78", {"start": v(-30.96, -1.5) * mm, "end": v(-28.16, -1.49) * mm});
            skLineSegment(sketch, "E79", {"start": v(-28.16, -1.49) * mm, "end": v(-28.16, 1.5) * mm});
            skLineSegment(sketch, "E80", {"start": v(-28.16, 1.5) * mm, "end": v(-30.96, 1.5) * mm});
            skLineSegment(sketch, "E81", {"start": v(-30.96, 1.5) * mm, "end": v(-30.96, -1.5) * mm});
            skLineSegment(sketch, "E82.1.0", {"start": v(-20.84, -22.95) * mm, "end": v(-18.86, -20.96) * mm});
            skArc(sketch, "E82.1.1", {"start": v(-28.16, 1.49) * mm, "mid": v(-28.2, 0) * mm, "end": v(-28.16, -1.49) * mm});
            skLineSegment(sketch, "E82.1.2", {"start": v(-20.98, -18.85) * mm, "end": v(-22.96, -20.83) * mm});
            skLineSegment(sketch, "E82.1.3", {"start": v(-22.96, -20.83) * mm, "end": v(-20.84, -22.95) * mm});
            skLineSegment(sketch, "E82.2.0", {"start": v(1.5, -30.96) * mm, "end": v(1.49, -28.16) * mm});
            skLineSegment(sketch, "E82.2.2", {"start": v(-1.5, -28.16) * mm, "end": v(-1.5, -30.96) * mm});
            skLineSegment(sketch, "E82.2.3", {"start": v(-1.5, -30.96) * mm, "end": v(1.5, -30.96) * mm});
            skLineSegment(sketch, "E82.3.0", {"start": v(22.95, -20.84) * mm, "end": v(20.96, -18.86) * mm});
            skLineSegment(sketch, "E82.3.2", {"start": v(18.85, -20.98) * mm, "end": v(20.83, -22.96) * mm});
            skLineSegment(sketch, "E82.3.3", {"start": v(20.83, -22.96) * mm, "end": v(22.95, -20.84) * mm});
            skLineSegment(sketch, "E82.4.0", {"start": v(30.96, 1.5) * mm, "end": v(28.16, 1.49) * mm});
            skArc(sketch, "E82.4.1", {"start": v(-28.16, 1.49) * mm, "mid": v(-28.2, 0) * mm, "end": v(-28.16, -1.49) * mm});
            skLineSegment(sketch, "E82.4.2", {"start": v(28.16, -1.5) * mm, "end": v(30.96, -1.5) * mm});
            skLineSegment(sketch, "E82.4.3", {"start": v(30.96, -1.5) * mm, "end": v(30.96, 1.5) * mm});
            skLineSegment(sketch, "E82.5.0", {"start": v(20.84, 22.95) * mm, "end": v(18.86, 20.96) * mm});
            skLineSegment(sketch, "E82.5.2", {"start": v(20.98, 18.85) * mm, "end": v(22.96, 20.83) * mm});
            skLineSegment(sketch, "E82.5.3", {"start": v(22.96, 20.83) * mm, "end": v(20.84, 22.95) * mm});
            skLineSegment(sketch, "E82.6.0", {"start": v(-1.5, 30.96) * mm, "end": v(-1.49, 28.16) * mm});
            skArc(sketch, "E82.6.1", {"start": v(-28.16, 1.49) * mm, "mid": v(-28.2, 0) * mm, "end": v(-28.16, -1.49) * mm});
            skLineSegment(sketch, "E82.6.2", {"start": v(1.5, 28.16) * mm, "end": v(1.5, 30.96) * mm});
            skLineSegment(sketch, "E82.6.3", {"start": v(1.5, 30.96) * mm, "end": v(-1.5, 30.96) * mm});
            skLineSegment(sketch, "E82.7.0", {"start": v(-22.95, 20.84) * mm, "end": v(-20.96, 18.86) * mm});
            skArc(sketch, "E82.7.1", {"start": v(-28.16, 1.49) * mm, "mid": v(-28.2, 0) * mm, "end": v(-28.16, -1.49) * mm});
            skLineSegment(sketch, "E82.7.2", {"start": v(-18.85, 20.98) * mm, "end": v(-20.83, 22.96) * mm});
            skLineSegment(sketch, "E82.7.3", {"start": v(-20.83, 22.96) * mm, "end": v(-22.95, 20.84) * mm});
            skLineSegment(sketch, "E83", {"start": v(1.49, -28.16) * mm, "end": v(-1.5, -28.16) * mm});
            skLineSegment(sketch, "E84", {"start": v(20.96, -18.86) * mm, "end": v(18.85, -20.98) * mm});
            skLineSegment(sketch, "E85", {"start": v(28.16, -1.5) * mm, "end": v(28.16, 1.49) * mm});
            skLineSegment(sketch, "E86", {"start": v(20.98, 18.85) * mm, "end": v(18.86, 20.96) * mm});
            skLineSegment(sketch, "E87", {"start": v(1.5, 28.16) * mm, "end": v(-1.49, 28.16) * mm});
            skLineSegment(sketch, "E88", {"start": v(-18.85, 20.98) * mm, "end": v(-20.96, 18.86) * mm});
            skLineSegment(sketch, "E89", {"start": v(-18.86, -20.96) * mm, "end": v(-20.98, -18.85) * mm});
            skSolve(sketch);
        }
        {
            var Q0;
            {var subQ45=sQuery(id+"F6.wireOp",EDGE,"E83");Q0=makeQuery(id+"F6.imprint","IMPRINT",FACE,{"disambiguationData":[TD([[makeQuery(id+"F6.imprint","IMPRINT",EDGE,{"derivedFrom":subQ45}),-1.0]])]});}
            extrude(context, id + "F7", {"entities" : qUnion([Q0]), "depth" : 3 * mm, "offsetDistance" : 25 * mm});
        }
        {
            var Q0;
            Q0=makeQuery(id+"F1.imprint","IMPRINT",FACE,{"disambiguationData":[TD([[makeQuery(id+"F1.imprint","IMPRINT",EDGE,{"derivedFrom":sQuery(id+"F1.wireOp",EDGE,"E3.7.0.0")}),1.0]])]});
            var Q1;
            Q1=makeQuery(id+"F1.imprint","IMPRINT",FACE,{"disambiguationData":[TD([[makeQuery(id+"F1.imprint","IMPRINT",EDGE,{"derivedFrom":sQuery(id+"F1.wireOp",EDGE,"E3.6.0.1")}),1.0]])]});
            var Q2;
            Q2=makeQuery(id+"F1.imprint","IMPRINT",FACE,{"disambiguationData":[TD([[makeQuery(id+"F1.imprint","IMPRINT",EDGE,{"derivedFrom":sQuery(id+"F1.wireOp",EDGE,"E3.5.0.1")}),1.0]])]});
            var Q3;
            Q3=makeQuery(id+"F1.imprint","IMPRINT",FACE,{"disambiguationData":[TD([[makeQuery(id+"F1.imprint","IMPRINT",EDGE,{"derivedFrom":sQuery(id+"F1.wireOp",EDGE,"E3.4.0.1")}),1.0]])]});
            var Q4;
            Q4=makeQuery(id+"F1.imprint","IMPRINT",FACE,{"disambiguationData":[TD([[makeQuery(id+"F1.imprint","IMPRINT",EDGE,{"derivedFrom":sQuery(id+"F1.wireOp",EDGE,"E3.3.0.1")}),1.0]])]});
            var Q5;
            Q5=makeQuery(id+"F1.imprint","IMPRINT",FACE,{"disambiguationData":[TD([[makeQuery(id+"F1.imprint","IMPRINT",EDGE,{"derivedFrom":sQuery(id+"F1.wireOp",EDGE,"E3.2.0.1")}),1.0]])]});
            var Q6;
            Q6=makeQuery(id+"F1.imprint","IMPRINT",FACE,{"disambiguationData":[TD([[makeQuery(id+"F1.imprint","IMPRINT",EDGE,{"derivedFrom":sQuery(id+"F1.wireOp",EDGE,"E3.1.0.1")}),1.0]])]});
            var Q7;
            Q7=makeQuery(id+"F1.imprint","IMPRINT",FACE,{"disambiguationData":[TD([[makeQuery(id+"F1.imprint","IMPRINT",EDGE,{"derivedFrom":sQuery(id+"F1.wireOp",EDGE,"E0")}),1.0]])]});
            extrude(context, id + "F8", {"entities" : qUnion([Q0, Q1, Q2, Q3, Q4, Q5, Q6, Q7]), "depth" : (getVariable(context, 'thickness')) * mm, "offsetDistance" : 25 * mm});
        }
        {
            var Q0;
            Q0=makeQuery(id+"F5.opExtrude","CAP_FACE",FACE,{"disambiguationData":[OSD([sQuery(id+"F4.wireOp",EDGE,"E66"),sQuery(id+"F4.wireOp",EDGE,"E67"),sQuery(id+"F4.wireOp",EDGE,"E68.bottom"),sQuery(id+"F4.wireOp",EDGE,"E68.top"),sQuery(id+"F4.wireOp",EDGE,"E68.left"),sQuery(id+"F4.wireOp",EDGE,"E68.right"),sQuery(id+"F4.wireOp",EDGE,"E69.1.0"),sQuery(id+"F4.wireOp",EDGE,"E69.1.1"),sQuery(id+"F4.wireOp",EDGE,"E69.1.2"),sQuery(id+"F4.wireOp",EDGE,"E69.1.3"),sQuery(id+"F4.wireOp",EDGE,"E69.2.0"),sQuery(id+"F4.wireOp",EDGE,"E69.2.1"),sQuery(id+"F4.wireOp",EDGE,"E69.2.2"),sQuery(id+"F4.wireOp",EDGE,"E69.2.3"),sQuery(id+"F4.wireOp",EDGE,"E69.3.0"),sQuery(id+"F4.wireOp",EDGE,"E69.3.1"),sQuery(id+"F4.wireOp",EDGE,"E69.3.2"),sQuery(id+"F4.wireOp",EDGE,"E69.3.3"),sQuery(id+"F4.wireOp",EDGE,"E69.4.0"),sQuery(id+"F4.wireOp",EDGE,"E69.4.1"),sQuery(id+"F4.wireOp",EDGE,"E69.4.2"),sQuery(id+"F4.wireOp",EDGE,"E69.4.3"),sQuery(id+"F4.wireOp",EDGE,"E69.5.0"),sQuery(id+"F4.wireOp",EDGE,"E69.5.1"),sQuery(id+"F4.wireOp",EDGE,"E69.5.2"),sQuery(id+"F4.wireOp",EDGE,"E69.5.3"),sQuery(id+"F4.wireOp",EDGE,"E69.6.0"),sQuery(id+"F4.wireOp",EDGE,"E69.6.1"),sQuery(id+"F4.wireOp",EDGE,"E69.6.2"),sQuery(id+"F4.wireOp",EDGE,"E69.6.3"),sQuery(id+"F4.wireOp",EDGE,"E69.7.0"),sQuery(id+"F4.wireOp",EDGE,"E69.7.1"),sQuery(id+"F4.wireOp",EDGE,"E69.7.2"),sQuery(id+"F4.wireOp",EDGE,"E69.7.3"),sQuery(id+"F4.wireOp",EDGE,"E70.bottom"),sQuery(id+"F4.wireOp",EDGE,"E70.top"),sQuery(id+"F4.wireOp",EDGE,"E70.left"),sQuery(id+"F4.wireOp",EDGE,"E70.right"),sQuery(id+"F4.wireOp",EDGE,"E71.filletArc"),sQuery(id+"F4.wireOp",EDGE,"E72.filletArc"),sQuery(id+"F4.wireOp",EDGE,"E73.filletArc"),sQuery(id+"F4.wireOp",EDGE,"E74.filletArc")])],"isStart":false});
            var sketch = newSketch(context, id + "F9", { "sketchPlane" : qUnion([Q0])});
            skArc(sketch, "E90", {"start": v(-5, 48.74) * mm, "mid": v(-42.44, 24.5) * mm, "end": v(-44.71, -20.04) * mm});
            skCircle(sketch, "E91", {"center": v(0, 0) * mm, "radius": 30.5 * mm});
            skLineSegment(sketch, "E92.top", {"start": v(5, 43.9) * mm, "end": v(-5, 43.9) * mm});
            skLineSegment(sketch, "E92.right", {"start": v(-5, 48.74) * mm, "end": v(-5, 43.9) * mm});
            skArc(sketch, "E93.MirrorC", {"start": v(-44.71, -20.04) * mm, "mid": v(-42.44, 24.5) * mm, "end": v(-5, 48.74) * mm});
            skLineSegment(sketch, "E94.MirrorCS", {"start": v(5, 48.74) * mm, "end": v(5, 43.9) * mm});
            skLineSegment(sketch, "E95.1.0", {"start": v(-39.71, -28.7) * mm, "end": v(-35.53, -26.28) * mm});
            skLineSegment(sketch, "E95.1.1", {"start": v(-40.52, -17.62) * mm, "end": v(-35.53, -26.28) * mm});
            skLineSegment(sketch, "E95.1.3", {"start": v(-44.71, -20.04) * mm, "end": v(-40.52, -17.62) * mm});
            skLineSegment(sketch, "E95.2.0", {"start": v(44.71, -20.04) * mm, "end": v(40.52, -17.62) * mm});
            skLineSegment(sketch, "E95.2.1", {"start": v(35.53, -26.28) * mm, "end": v(40.52, -17.62) * mm});
            skLineSegment(sketch, "E95.2.3", {"start": v(39.71, -28.7) * mm, "end": v(35.53, -26.28) * mm});
            skPoint(sketch, "E92.bottom.start.orphan", {"position": v(0, 49) * mm});
            skArc(sketch, "E96.trimOffspring", {"start": v(-39.71, -28.7) * mm, "mid": v(0, -49) * mm, "end": v(39.71, -28.7) * mm});
            skArc(sketch, "E97.trimOffspring", {"start": v(44.71, -20.04) * mm, "mid": v(42.44, 24.5) * mm, "end": v(5, 48.74) * mm});
            skArc(sketch, "E98.trimOffspring", {"start": v(39.71, -28.7) * mm, "mid": v(0, -49) * mm, "end": v(-39.71, -28.7) * mm});
            skPoint(sketch, "E99.orphan", {"position": v(39.94, -28.83) * mm});
            skPoint(sketch, "E100.orphan", {"position": v(44.94, -20.17) * mm});
            skPoint(sketch, "E101.orphan", {"position": v(-39.94, -28.83) * mm});
            skPoint(sketch, "E102.orphan", {"position": v(-44.94, -20.17) * mm});
            skArc(sketch, "E103.trimOffspring", {"start": v(5, 48.74) * mm, "mid": v(42.44, 24.5) * mm, "end": v(44.71, -20.04) * mm});
            skPoint(sketch, "E104.orphan", {"position": v(-5, 49) * mm});
            skPoint(sketch, "E105.orphan", {"position": v(5, 49) * mm});
            skPoint(sketch, "E106.orphan", {"position": v(-38.08, -21.86) * mm});
            skPoint(sketch, "E107.orphan", {"position": v(37.97, -22.04) * mm});
            skSolve(sketch);
        }
        {
            var Q0;
            Q0=makeQuery(id+"F9.imprint","IMPRINT",FACE,{"disambiguationData":[TD([[makeQuery(id+"F9.imprint","IMPRINT",EDGE,{"derivedFrom":sQuery(id+"F9.wireOp",EDGE,"E92.top")}),1.0]])]});
            var Q1;
            Q1=makeQuery(id+"F9.imprint","IMPRINT",FACE,{"disambiguationData":[TD([[makeQuery(id+"F9.imprint","IMPRINT",EDGE,{"derivedFrom":makeQuery(id+"F5.opExtrude","CAP_EDGE",EDGE,{"disambiguationData":[OSD([sQuery(id+"F4.wireOp",EDGE,"E66")])],"isStart":false})}),1.0]])]});
            extrude(context, id + "F10", {"entities" : qUnion([Q0, Q1]), "depth" : 2 * mm, "offsetDistance" : 25 * mm});
        }
        {
            var Q0;
            Q0=makeQuery(id+"F7.opExtrude","CAP_FACE",FACE,{"disambiguationData":[OSD([sQuery(id+"F4.wireOp",EDGE,"E68.bottom"),sQuery(id+"F4.wireOp",EDGE,"E68.left"),sQuery(id+"F4.wireOp",EDGE,"E69.1.0"),sQuery(id+"F4.wireOp",EDGE,"E69.1.1"),sQuery(id+"F4.wireOp",EDGE,"E69.2.0"),sQuery(id+"F4.wireOp",EDGE,"E69.2.1"),sQuery(id+"F4.wireOp",EDGE,"E69.3.0"),sQuery(id+"F4.wireOp",EDGE,"E69.3.1"),sQuery(id+"F4.wireOp",EDGE,"E69.4.0"),sQuery(id+"F4.wireOp",EDGE,"E69.4.1"),sQuery(id+"F4.wireOp",EDGE,"E69.5.0"),sQuery(id+"F4.wireOp",EDGE,"E69.5.1"),sQuery(id+"F4.wireOp",EDGE,"E69.6.0"),sQuery(id+"F4.wireOp",EDGE,"E69.6.1"),sQuery(id+"F4.wireOp",EDGE,"E69.7.0"),sQuery(id+"F4.wireOp",EDGE,"E69.7.1"),sQuery(id+"F4.wireOp",EDGE,"E70.bottom"),sQuery(id+"F4.wireOp",EDGE,"E70.top"),sQuery(id+"F4.wireOp",EDGE,"E70.left"),sQuery(id+"F4.wireOp",EDGE,"E70.right"),sQuery(id+"F4.wireOp",EDGE,"E71.filletArc"),sQuery(id+"F4.wireOp",EDGE,"E72.filletArc"),sQuery(id+"F4.wireOp",EDGE,"E73.filletArc"),sQuery(id+"F4.wireOp",EDGE,"E74.filletArc"),sQuery(id+"F6.wireOp",EDGE,"E75"),sQuery(id+"F6.wireOp",EDGE,"E76"),sQuery(id+"F6.wireOp",EDGE,"E78"),sQuery(id+"F6.wireOp",EDGE,"E79"),sQuery(id+"F6.wireOp",EDGE,"E80"),sQuery(id+"F6.wireOp",EDGE,"E82.1.0"),sQuery(id+"F6.wireOp",EDGE,"E82.1.2"),sQuery(id+"F6.wireOp",EDGE,"E82.2.0"),sQuery(id+"F6.wireOp",EDGE,"E82.2.2"),sQuery(id+"F6.wireOp",EDGE,"E82.3.0"),sQuery(id+"F6.wireOp",EDGE,"E82.3.2"),sQuery(id+"F6.wireOp",EDGE,"E82.4.0"),sQuery(id+"F6.wireOp",EDGE,"E82.4.2"),sQuery(id+"F6.wireOp",EDGE,"E82.5.0"),sQuery(id+"F6.wireOp",EDGE,"E82.5.2"),sQuery(id+"F6.wireOp",EDGE,"E82.6.0"),sQuery(id+"F6.wireOp",EDGE,"E82.6.2"),sQuery(id+"F6.wireOp",EDGE,"E82.7.0"),sQuery(id+"F6.wireOp",EDGE,"E82.7.2"),sQuery(id+"F6.wireOp",EDGE,"E83"),sQuery(id+"F6.wireOp",EDGE,"E84"),sQuery(id+"F6.wireOp",EDGE,"E85"),sQuery(id+"F6.wireOp",EDGE,"E86"),sQuery(id+"F6.wireOp",EDGE,"E87"),sQuery(id+"F6.wireOp",EDGE,"E88"),sQuery(id+"F6.wireOp",EDGE,"E89")])],"isStart":false});
            var sketch = newSketch(context, id + "F11", { "sketchPlane" : qUnion([Q0])});
            skArc(sketch, "E108", {"start": v(-37.37, 6.75) * mm, "mid": v(0, -38.14) * mm, "end": v(37.37, 6.75) * mm});
            skLineSegment(sketch, "E109.bottom", {"start": v(23.5, -17.64) * mm, "end": v(-23.5, -17.64) * mm});
            skLineSegment(sketch, "E109.left", {"start": v(25.5, -15.64) * mm, "end": v(25.5, 1.5) * mm});
            skLineSegment(sketch, "E109.right", {"start": v(-25.5, -15.64) * mm, "end": v(-25.5, 1.5) * mm});
            skPoint(sketch, "E110.visualSharp", {"position": v(-25.5, 17.36) * mm});
            skPoint(sketch, "E111.visualSharp", {"position": v(25.5, -17.64) * mm});
            skArc(sketch, "E111.filletArc", {"start": v(23.5, -17.64) * mm, "mid": v(24.91, -17.05) * mm, "end": v(25.5, -15.64) * mm});
            skPoint(sketch, "E112.visualSharp", {"position": v(25.5, 17.36) * mm});
            skPoint(sketch, "E113.visualSharp", {"position": v(-25.5, -17.64) * mm});
            skArc(sketch, "E113.filletArc", {"start": v(-25.5, -15.64) * mm, "mid": v(-24.92, -17.05) * mm, "end": v(-23.5, -17.64) * mm});
            skLineSegment(sketch, "E114", {"start": v(-37.37, 6.75) * mm, "end": v(37.37, 6.75) * mm});
            skLineSegment(sketch, "E115", {"start": v(-25.5, 1.5) * mm, "end": v(25.5, 1.5) * mm});
            skSolve(sketch);
        }
        {
            var Q0;
            {var subQ18=sQuery(id+"F11.wireOp",EDGE,"E108");Q0=makeQuery(id+"F11.imprint","IMPRINT",FACE,{"disambiguationData":[TD([[makeQuery(id+"F11.imprint","IMPRINT",EDGE,{"derivedFrom":subQ18}),1.0]])]});}
            var Q1;
            {var subQ0=sQuery(id+"F11.wireOp",EDGE,"E109.bottom");var subQ1=sQuery(id+"F6.wireOp",EDGE,"E75");var subQ2=sQuery(id+"F4.wireOp",EDGE,"E70.bottom");var subQ4=makeQuery(id+"F7.opExtrude","CAP_EDGE",EDGE,{"disambiguationData":[OSD([subQ1]),TDD([makeQuery(id+"F6.imprint","IMPRINT",EDGE,{"disambiguationData":[TD([[makeQuery(id+"F6.imprint","INTERSECT",VERTEX,{"derivedFrom":[makeQuery(id+"F5.opExtrude","CAP_EDGE",EDGE,{"disambiguationData":[OSD([subQ2]),TDD([makeQuery(id+"F4.imprint","IMPRINT",EDGE,{"disambiguationData":[TD([[makeQuery(id+"F4.imprint","INTERSECT",VERTEX,{"derivedFrom":[subQ2,sQuery(id+"F4.wireOp",EDGE,"E74.filletArc")]}),1.0]])],"derivedFrom":subQ2})])],"isStart":false}),subQ1]}),-1.0]])],"derivedFrom":subQ1})])],"isStart":false});var subQ5=makeQuery(id+"F11.imprint","INTERSECT",VERTEX,{"disambiguationData":[OD(0.0)],"derivedFrom":[subQ4,subQ0]});Q1=makeQuery(id+"F11.imprint","IMPRINT",FACE,{"disambiguationData":[TD([[makeQuery(id+"F11.imprint","IMPRINT",EDGE,{"disambiguationData":[TD([[subQ5,-1.0]])],"derivedFrom":subQ0}),1.0]])]});}
            var Q2;
            {var subQ12=sQuery(id+"F11.wireOp",EDGE,"E115");Q2=makeQuery(id+"F11.imprint","IMPRINT",FACE,{"disambiguationData":[TD([[makeQuery(id+"F11.imprint","IMPRINT",EDGE,{"derivedFrom":subQ12}),1.0]])]});}
            var Q3;
            {var subQ19=sQuery(id+"F11.wireOp",EDGE,"E111.filletArc");Q3=makeQuery(id+"F11.imprint","IMPRINT",FACE,{"disambiguationData":[TD([[makeQuery(id+"F11.imprint","IMPRINT",EDGE,{"derivedFrom":subQ19}),-1.0]])]});}
            extrude(context, id + "F12", {"entities" : qUnion([Q0, Q1, Q2, Q3]), "depth" : 2 * mm, "offsetDistance" : 25 * mm});
        }
        {
            var Q0;
            Q0=makeQuery(id+"F9.imprint","IMPRINT",FACE,{"disambiguationData":[TD([[makeQuery(id+"F9.imprint","IMPRINT",EDGE,{"derivedFrom":sQuery(id+"F9.wireOp",EDGE,"E92.top")}),1.0]])]});
            var Q1;
            Q1=makeQuery(id+"F9.imprint","IMPRINT",FACE,{"disambiguationData":[TD([[makeQuery(id+"F9.imprint","IMPRINT",EDGE,{"derivedFrom":makeQuery(id+"F5.opExtrude","CAP_EDGE",EDGE,{"disambiguationData":[OSD([sQuery(id+"F4.wireOp",EDGE,"E66")])],"isStart":false})}),1.0]])]});
            extrude(context, id + "F13", {"entities" : qUnion([Q0, Q1]), "depth" : 2 * mm, "offsetDistance" : 25 * mm});
        }
    });
